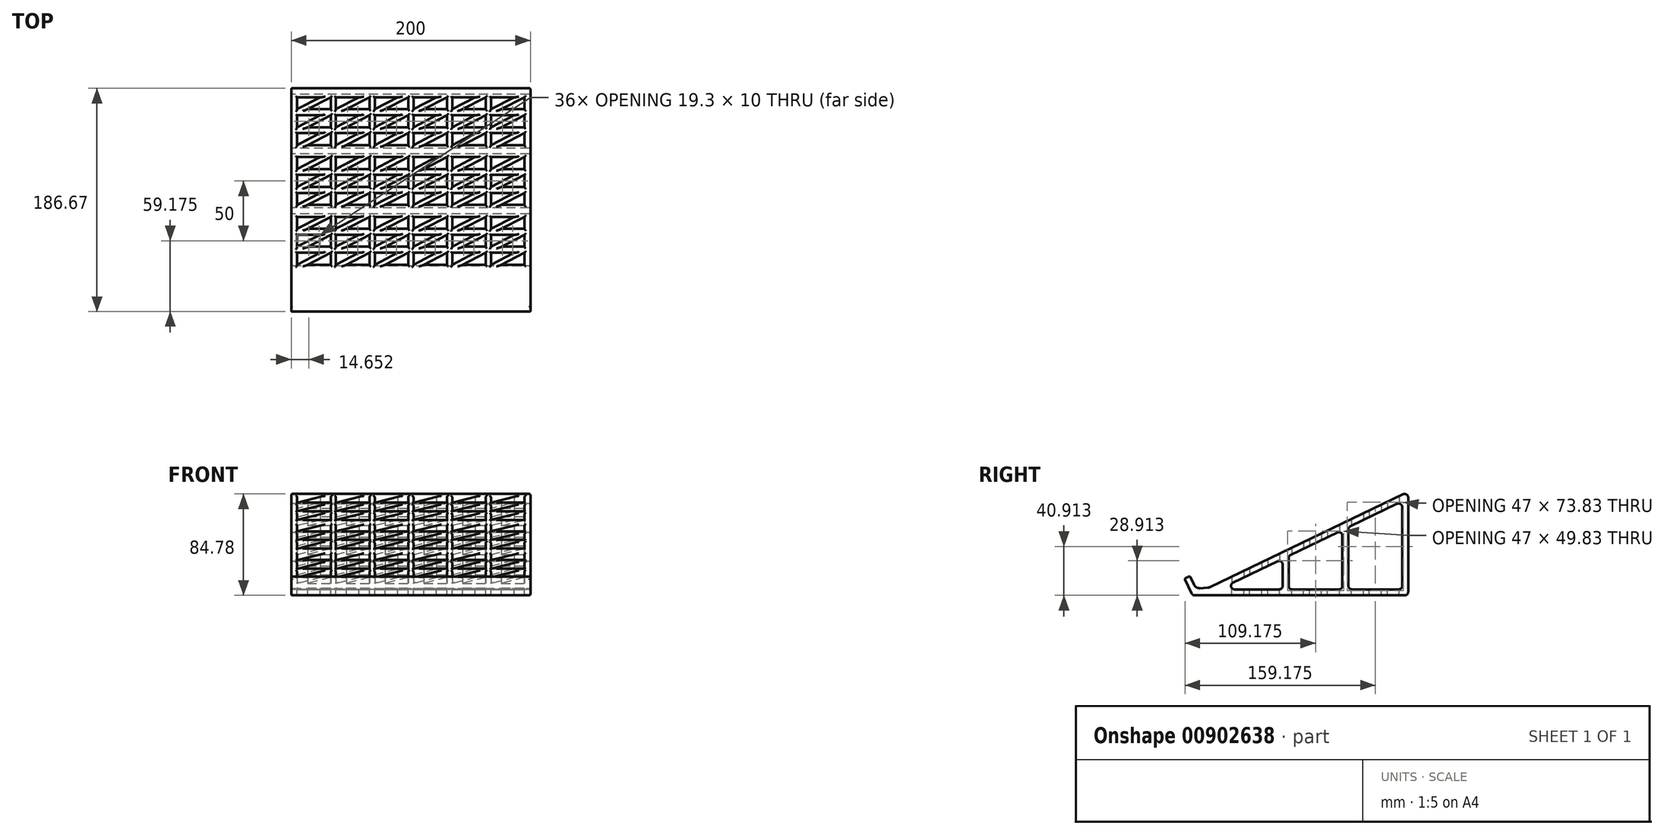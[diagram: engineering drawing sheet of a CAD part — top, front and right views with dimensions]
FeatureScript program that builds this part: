
annotation { "Feature Type Name" : "Feature", "Feature Type Description" : "" }
export const myFeature = defineFeature(function(context is Context, id is Id, definition is map)
    precondition{}
    {
        {
            var Q0;
            Q0=qCreatedBy(makeId("Right.planeOp"),FACE);
            var sketch = newSketch(context, id + "F0", { "sketchPlane" : qUnion([Q0])});
            skLineSegment(sketch, "E0", {"start": v(0, 0) * mm, "end": v(250, 120) * mm});
            skLineSegment(sketch, "E1", {"start": v(250, 120) * mm, "end": v(242.21, 136.23) * mm});
            skLineSegment(sketch, "E2", {"start": v(242.21, 136.23) * mm, "end": v(-7.79, 16.23) * mm});
            skLineSegment(sketch, "E3", {"start": v(-7.79, 16.23) * mm, "end": v(0, 0) * mm});
            skSolve(sketch);
        }
        {
            var Q0;
            Q0=qCreatedBy(makeId("Right.planeOp"),FACE);
            var sketch = newSketch(context, id + "F1", { "sketchPlane" : qUnion([Q0])});
            skLineSegment(sketch, "E4", {"start": v(0, 0) * mm, "end": v(180.3, 86.55) * mm});
            skLineSegment(sketch, "E5", {"start": v(180.3, 86.55) * mm, "end": v(180.3, 0) * mm});
            skLineSegment(sketch, "E6", {"start": v(180.3, 0) * mm, "end": v(0, 0) * mm});
            skLineSegment(sketch, "E7", {"start": v(0, 0) * mm, "end": v(-6.7, 13.97) * mm});
            skLineSegment(sketch, "E8", {"start": v(-6.7, 13.97) * mm, "end": v(-2.2, 16.14) * mm});
            skLineSegment(sketch, "E9", {"start": v(-2.2, 16.14) * mm, "end": v(4.5, 2.16) * mm});
            skLineSegment(sketch, "E10", {"start": v(75.3, 30.6) * mm, "end": v(75.3, 5) * mm});
            skLineSegment(sketch, "E11", {"start": v(75.3, 5) * mm, "end": v(21.97, 5) * mm});
            skLineSegment(sketch, "E12", {"start": v(21.97, 5) * mm, "end": v(75.3, 30.6) * mm});
            skLineSegment(sketch, "E13", {"start": v(175.3, 78.6) * mm, "end": v(130.3, 57) * mm});
            skLineSegment(sketch, "E14", {"start": v(175.3, 5) * mm, "end": v(175.3, 78.6) * mm});
            skLineSegment(sketch, "E15", {"start": v(125.3, 54.6) * mm, "end": v(125.3, 5) * mm});
            skLineSegment(sketch, "E16", {"start": v(80.3, 5) * mm, "end": v(125.3, 5) * mm});
            skLineSegment(sketch, "E17", {"start": v(80.3, 5) * mm, "end": v(80.3, 33) * mm});
            skLineSegment(sketch, "E18", {"start": v(80.3, 33) * mm, "end": v(125.3, 54.6) * mm});
            skLineSegment(sketch, "E19", {"start": v(130.3, 57) * mm, "end": v(130.3, 5) * mm});
            skLineSegment(sketch, "E20", {"start": v(130.3, 5) * mm, "end": v(175.3, 5) * mm});
            skSolve(sketch);
        }
        {
            var Q0;
            Q0=makeQuery(id+"F1.imprint","IMPRINT",FACE,{"disambiguationData":[TD([[makeQuery(id+"F1.imprint","IMPRINT",EDGE,{"derivedFrom":sQuery(id+"F1.wireOp",EDGE,"E4")}),-1.0]])]});
            var Q1;
            {var subQ0=sQuery(id+"F1.wireOp",EDGE,"E7");Q1=makeQuery(id+"F1.imprint","IMPRINT",FACE,{"disambiguationData":[TD([[makeQuery(id+"F1.imprint","IMPRINT",EDGE,{"derivedFrom":subQ0}),-1.0]])]});}
            extrude(context, id + "F2", {"entities" : qUnion([Q0, Q1]), "endBound" : BoundingType.SYMMETRIC, "depth" : 200 * mm, "offsetDistance" : 25 * mm});
        }
        {
            var Q0;
            Q0=makeQuery(id+"F2.opExtrude","SWEPT_FACE",FACE,{"disambiguationData":[OSD([sQuery(id+"F1.wireOp",EDGE,"E20")])]});
            var sketch = newSketch(context, id + "F3", { "sketchPlane" : qUnion([Q0])});
            skLineSegment(sketch, "E21", {"start": v(-95, 162.8) * mm, "end": v(-95, 172.8) * mm});
            skLineSegment(sketch, "E22", {"start": v(-95, 172.8) * mm, "end": v(-75.7, 172.8) * mm});
            skLineSegment(sketch, "E23", {"start": v(-75.7, 172.8) * mm, "end": v(-95, 162.8) * mm});
            skLineSegment(sketch, "E24", {"start": v(-86.3, 162.8) * mm, "end": v(-67, 172.8) * mm});
            skLineSegment(sketch, "E25", {"start": v(-67, 172.8) * mm, "end": v(-67, 162.8) * mm});
            skLineSegment(sketch, "E26", {"start": v(-67, 162.8) * mm, "end": v(-86.3, 162.8) * mm});
            skLineSegment(sketch, "E27.0.1.0", {"start": v(-67, 147.8) * mm, "end": v(-86.3, 147.8) * mm});
            skLineSegment(sketch, "E27.0.1.1", {"start": v(-86.3, 147.8) * mm, "end": v(-67, 157.8) * mm});
            skLineSegment(sketch, "E27.0.1.2", {"start": v(-95, 157.8) * mm, "end": v(-75.7, 157.8) * mm});
            skLineSegment(sketch, "E27.0.1.3", {"start": v(-75.7, 157.8) * mm, "end": v(-95, 147.8) * mm});
            skLineSegment(sketch, "E27.0.1.4", {"start": v(-67, 157.8) * mm, "end": v(-67, 147.8) * mm});
            skLineSegment(sketch, "E27.0.1.5", {"start": v(-95, 147.8) * mm, "end": v(-95, 157.8) * mm});
            skLineSegment(sketch, "E27.0.2.0", {"start": v(-67, 132.8) * mm, "end": v(-86.3, 132.8) * mm});
            skLineSegment(sketch, "E27.0.2.1", {"start": v(-86.3, 132.8) * mm, "end": v(-67, 142.8) * mm});
            skLineSegment(sketch, "E27.0.2.2", {"start": v(-95, 142.8) * mm, "end": v(-75.7, 142.8) * mm});
            skLineSegment(sketch, "E27.0.2.3", {"start": v(-75.7, 142.8) * mm, "end": v(-95, 132.8) * mm});
            skLineSegment(sketch, "E27.0.2.4", {"start": v(-67, 142.8) * mm, "end": v(-67, 132.8) * mm});
            skLineSegment(sketch, "E27.0.2.5", {"start": v(-95, 132.8) * mm, "end": v(-95, 142.8) * mm});
            skLineSegment(sketch, "E27.1.0.0", {"start": v(-34.6, 162.8) * mm, "end": v(-53.9, 162.8) * mm});
            skLineSegment(sketch, "E27.1.0.1", {"start": v(-53.9, 162.8) * mm, "end": v(-34.6, 172.8) * mm});
            skLineSegment(sketch, "E27.1.0.2", {"start": v(-62.6, 172.8) * mm, "end": v(-43.3, 172.8) * mm});
            skLineSegment(sketch, "E27.1.0.3", {"start": v(-43.3, 172.8) * mm, "end": v(-62.6, 162.8) * mm});
            skLineSegment(sketch, "E27.1.0.4", {"start": v(-34.6, 172.8) * mm, "end": v(-34.6, 162.8) * mm});
            skLineSegment(sketch, "E27.1.0.5", {"start": v(-62.6, 162.8) * mm, "end": v(-62.6, 172.8) * mm});
            skLineSegment(sketch, "E27.1.1.0", {"start": v(-34.6, 147.8) * mm, "end": v(-53.9, 147.8) * mm});
            skLineSegment(sketch, "E27.1.1.1", {"start": v(-53.9, 147.8) * mm, "end": v(-34.6, 157.8) * mm});
            skLineSegment(sketch, "E27.1.1.2", {"start": v(-62.6, 157.8) * mm, "end": v(-43.3, 157.8) * mm});
            skLineSegment(sketch, "E27.1.1.3", {"start": v(-43.3, 157.8) * mm, "end": v(-62.6, 147.8) * mm});
            skLineSegment(sketch, "E27.1.1.4", {"start": v(-34.6, 157.8) * mm, "end": v(-34.6, 147.8) * mm});
            skLineSegment(sketch, "E27.1.1.5", {"start": v(-62.6, 147.8) * mm, "end": v(-62.6, 157.8) * mm});
            skLineSegment(sketch, "E27.1.2.0", {"start": v(-34.6, 132.8) * mm, "end": v(-53.9, 132.8) * mm});
            skLineSegment(sketch, "E27.1.2.1", {"start": v(-53.9, 132.8) * mm, "end": v(-34.6, 142.8) * mm});
            skLineSegment(sketch, "E27.1.2.2", {"start": v(-62.6, 142.8) * mm, "end": v(-43.3, 142.8) * mm});
            skLineSegment(sketch, "E27.1.2.3", {"start": v(-43.3, 142.8) * mm, "end": v(-62.6, 132.8) * mm});
            skLineSegment(sketch, "E27.1.2.4", {"start": v(-34.6, 142.8) * mm, "end": v(-34.6, 132.8) * mm});
            skLineSegment(sketch, "E27.1.2.5", {"start": v(-62.6, 132.8) * mm, "end": v(-62.6, 142.8) * mm});
            skLineSegment(sketch, "E27.2.0.0", {"start": v(-2.2, 162.8) * mm, "end": v(-21.5, 162.8) * mm});
            skLineSegment(sketch, "E27.2.0.1", {"start": v(-21.5, 162.8) * mm, "end": v(-2.2, 172.8) * mm});
            skLineSegment(sketch, "E27.2.0.2", {"start": v(-30.2, 172.8) * mm, "end": v(-10.9, 172.8) * mm});
            skLineSegment(sketch, "E27.2.0.3", {"start": v(-10.9, 172.8) * mm, "end": v(-30.2, 162.8) * mm});
            skLineSegment(sketch, "E27.2.0.4", {"start": v(-2.2, 172.8) * mm, "end": v(-2.2, 162.8) * mm});
            skLineSegment(sketch, "E27.2.0.5", {"start": v(-30.2, 162.8) * mm, "end": v(-30.2, 172.8) * mm});
            skLineSegment(sketch, "E27.2.1.0", {"start": v(-2.2, 147.8) * mm, "end": v(-21.5, 147.8) * mm});
            skLineSegment(sketch, "E27.2.1.1", {"start": v(-21.5, 147.8) * mm, "end": v(-2.2, 157.8) * mm});
            skLineSegment(sketch, "E27.2.1.2", {"start": v(-30.2, 157.8) * mm, "end": v(-10.9, 157.8) * mm});
            skLineSegment(sketch, "E27.2.1.3", {"start": v(-10.9, 157.8) * mm, "end": v(-30.2, 147.8) * mm});
            skLineSegment(sketch, "E27.2.1.4", {"start": v(-2.2, 157.8) * mm, "end": v(-2.2, 147.8) * mm});
            skLineSegment(sketch, "E27.2.1.5", {"start": v(-30.2, 147.8) * mm, "end": v(-30.2, 157.8) * mm});
            skLineSegment(sketch, "E27.2.2.0", {"start": v(-2.2, 132.8) * mm, "end": v(-21.5, 132.8) * mm});
            skLineSegment(sketch, "E27.2.2.1", {"start": v(-21.5, 132.8) * mm, "end": v(-2.2, 142.8) * mm});
            skLineSegment(sketch, "E27.2.2.2", {"start": v(-30.2, 142.8) * mm, "end": v(-10.9, 142.8) * mm});
            skLineSegment(sketch, "E27.2.2.3", {"start": v(-10.9, 142.8) * mm, "end": v(-30.2, 132.8) * mm});
            skLineSegment(sketch, "E27.2.2.4", {"start": v(-2.2, 142.8) * mm, "end": v(-2.2, 132.8) * mm});
            skLineSegment(sketch, "E27.2.2.5", {"start": v(-30.2, 132.8) * mm, "end": v(-30.2, 142.8) * mm});
            skLineSegment(sketch, "E27.3.0.0", {"start": v(30.2, 162.8) * mm, "end": v(10.9, 162.8) * mm});
            skLineSegment(sketch, "E27.3.0.1", {"start": v(10.9, 162.8) * mm, "end": v(30.2, 172.8) * mm});
            skLineSegment(sketch, "E27.3.0.2", {"start": v(2.2, 172.8) * mm, "end": v(21.5, 172.8) * mm});
            skLineSegment(sketch, "E27.3.0.3", {"start": v(21.5, 172.8) * mm, "end": v(2.2, 162.8) * mm});
            skLineSegment(sketch, "E27.3.0.4", {"start": v(30.2, 172.8) * mm, "end": v(30.2, 162.8) * mm});
            skLineSegment(sketch, "E27.3.0.5", {"start": v(2.2, 162.8) * mm, "end": v(2.2, 172.8) * mm});
            skLineSegment(sketch, "E27.3.1.0", {"start": v(30.2, 147.8) * mm, "end": v(10.9, 147.8) * mm});
            skLineSegment(sketch, "E27.3.1.1", {"start": v(10.9, 147.8) * mm, "end": v(30.2, 157.8) * mm});
            skLineSegment(sketch, "E27.3.1.2", {"start": v(2.2, 157.8) * mm, "end": v(21.5, 157.8) * mm});
            skLineSegment(sketch, "E27.3.1.3", {"start": v(21.5, 157.8) * mm, "end": v(2.2, 147.8) * mm});
            skLineSegment(sketch, "E27.3.1.4", {"start": v(30.2, 157.8) * mm, "end": v(30.2, 147.8) * mm});
            skLineSegment(sketch, "E27.3.1.5", {"start": v(2.2, 147.8) * mm, "end": v(2.2, 157.8) * mm});
            skLineSegment(sketch, "E27.3.2.0", {"start": v(30.2, 132.8) * mm, "end": v(10.9, 132.8) * mm});
            skLineSegment(sketch, "E27.3.2.1", {"start": v(10.9, 132.8) * mm, "end": v(30.2, 142.8) * mm});
            skLineSegment(sketch, "E27.3.2.2", {"start": v(2.2, 142.8) * mm, "end": v(21.5, 142.8) * mm});
            skLineSegment(sketch, "E27.3.2.3", {"start": v(21.5, 142.8) * mm, "end": v(2.2, 132.8) * mm});
            skLineSegment(sketch, "E27.3.2.4", {"start": v(30.2, 142.8) * mm, "end": v(30.2, 132.8) * mm});
            skLineSegment(sketch, "E27.3.2.5", {"start": v(2.2, 132.8) * mm, "end": v(2.2, 142.8) * mm});
            skLineSegment(sketch, "E27.4.0.0", {"start": v(62.6, 162.8) * mm, "end": v(43.3, 162.8) * mm});
            skLineSegment(sketch, "E27.4.0.1", {"start": v(43.3, 162.8) * mm, "end": v(62.6, 172.8) * mm});
            skLineSegment(sketch, "E27.4.0.2", {"start": v(34.6, 172.8) * mm, "end": v(53.9, 172.8) * mm});
            skLineSegment(sketch, "E27.4.0.3", {"start": v(53.9, 172.8) * mm, "end": v(34.6, 162.8) * mm});
            skLineSegment(sketch, "E27.4.0.4", {"start": v(62.6, 172.8) * mm, "end": v(62.6, 162.8) * mm});
            skLineSegment(sketch, "E27.4.0.5", {"start": v(34.6, 162.8) * mm, "end": v(34.6, 172.8) * mm});
            skLineSegment(sketch, "E27.4.1.0", {"start": v(62.6, 147.8) * mm, "end": v(43.3, 147.8) * mm});
            skLineSegment(sketch, "E27.4.1.1", {"start": v(43.3, 147.8) * mm, "end": v(62.6, 157.8) * mm});
            skLineSegment(sketch, "E27.4.1.2", {"start": v(34.6, 157.8) * mm, "end": v(53.9, 157.8) * mm});
            skLineSegment(sketch, "E27.4.1.3", {"start": v(53.9, 157.8) * mm, "end": v(34.6, 147.8) * mm});
            skLineSegment(sketch, "E27.4.1.4", {"start": v(62.6, 157.8) * mm, "end": v(62.6, 147.8) * mm});
            skLineSegment(sketch, "E27.4.1.5", {"start": v(34.6, 147.8) * mm, "end": v(34.6, 157.8) * mm});
            skLineSegment(sketch, "E27.4.2.0", {"start": v(62.6, 132.8) * mm, "end": v(43.3, 132.8) * mm});
            skLineSegment(sketch, "E27.4.2.1", {"start": v(43.3, 132.8) * mm, "end": v(62.6, 142.8) * mm});
            skLineSegment(sketch, "E27.4.2.2", {"start": v(34.6, 142.8) * mm, "end": v(53.9, 142.8) * mm});
            skLineSegment(sketch, "E27.4.2.3", {"start": v(53.9, 142.8) * mm, "end": v(34.6, 132.8) * mm});
            skLineSegment(sketch, "E27.4.2.4", {"start": v(62.6, 142.8) * mm, "end": v(62.6, 132.8) * mm});
            skLineSegment(sketch, "E27.4.2.5", {"start": v(34.6, 132.8) * mm, "end": v(34.6, 142.8) * mm});
            skLineSegment(sketch, "E27.5.0.0", {"start": v(95, 162.8) * mm, "end": v(75.7, 162.8) * mm});
            skLineSegment(sketch, "E27.5.0.1", {"start": v(75.7, 162.8) * mm, "end": v(95, 172.8) * mm});
            skLineSegment(sketch, "E27.5.0.2", {"start": v(67, 172.8) * mm, "end": v(86.3, 172.8) * mm});
            skLineSegment(sketch, "E27.5.0.3", {"start": v(86.3, 172.8) * mm, "end": v(67, 162.8) * mm});
            skLineSegment(sketch, "E27.5.0.4", {"start": v(95, 172.8) * mm, "end": v(95, 162.8) * mm});
            skLineSegment(sketch, "E27.5.0.5", {"start": v(67, 162.8) * mm, "end": v(67, 172.8) * mm});
            skLineSegment(sketch, "E27.5.1.0", {"start": v(95, 147.8) * mm, "end": v(75.7, 147.8) * mm});
            skLineSegment(sketch, "E27.5.1.1", {"start": v(75.7, 147.8) * mm, "end": v(95, 157.8) * mm});
            skLineSegment(sketch, "E27.5.1.2", {"start": v(67, 157.8) * mm, "end": v(86.3, 157.8) * mm});
            skLineSegment(sketch, "E27.5.1.3", {"start": v(86.3, 157.8) * mm, "end": v(67, 147.8) * mm});
            skLineSegment(sketch, "E27.5.1.4", {"start": v(95, 157.8) * mm, "end": v(95, 147.8) * mm});
            skLineSegment(sketch, "E27.5.1.5", {"start": v(67, 147.8) * mm, "end": v(67, 157.8) * mm});
            skLineSegment(sketch, "E27.5.2.0", {"start": v(95, 132.8) * mm, "end": v(75.7, 132.8) * mm});
            skLineSegment(sketch, "E27.5.2.1", {"start": v(75.7, 132.8) * mm, "end": v(95, 142.8) * mm});
            skLineSegment(sketch, "E27.5.2.2", {"start": v(67, 142.8) * mm, "end": v(86.3, 142.8) * mm});
            skLineSegment(sketch, "E27.5.2.3", {"start": v(86.3, 142.8) * mm, "end": v(67, 132.8) * mm});
            skLineSegment(sketch, "E27.5.2.4", {"start": v(95, 142.8) * mm, "end": v(95, 132.8) * mm});
            skLineSegment(sketch, "E27.5.2.5", {"start": v(67, 132.8) * mm, "end": v(67, 142.8) * mm});
            skLineSegment(sketch, "E27.direction1", {"start": v(-95, 162.8) * mm, "end": v(-62.6, 162.8) * mm, "construction": true});
            skLineSegment(sketch, "E27.direction2", {"start": v(-95, 162.8) * mm, "end": v(-95, 147.8) * mm, "construction": true});
            skLineSegment(sketch, "E28.0.1.0", {"start": v(34.6, 112.8) * mm, "end": v(34.6, 122.8) * mm});
            skLineSegment(sketch, "E28.0.1.1", {"start": v(-34.6, 82.8) * mm, "end": v(-53.9, 82.8) * mm});
            skLineSegment(sketch, "E28.0.1.2", {"start": v(-10.9, 92.8) * mm, "end": v(-30.2, 82.8) * mm});
            skLineSegment(sketch, "E28.0.1.3", {"start": v(34.6, 82.8) * mm, "end": v(34.6, 92.8) * mm});
            skLineSegment(sketch, "E28.0.1.4", {"start": v(-2.2, 97.8) * mm, "end": v(-21.5, 97.8) * mm});
            skLineSegment(sketch, "E28.0.1.5", {"start": v(-75.7, 107.8) * mm, "end": v(-95, 97.8) * mm});
            skLineSegment(sketch, "E28.0.1.6", {"start": v(-95, 122.8) * mm, "end": v(-75.7, 122.8) * mm});
            skLineSegment(sketch, "E28.0.1.7", {"start": v(30.2, 112.8) * mm, "end": v(10.9, 112.8) * mm});
            skLineSegment(sketch, "E28.0.1.8", {"start": v(-2.2, 92.8) * mm, "end": v(-2.2, 82.8) * mm});
            skLineSegment(sketch, "E28.0.1.9", {"start": v(-86.3, 112.8) * mm, "end": v(-67, 122.8) * mm});
            skLineSegment(sketch, "E28.0.1.10", {"start": v(-34.6, 107.8) * mm, "end": v(-34.6, 97.8) * mm});
            skLineSegment(sketch, "E28.0.1.11", {"start": v(-62.6, 97.8) * mm, "end": v(-62.6, 107.8) * mm});
            skLineSegment(sketch, "E28.0.1.12", {"start": v(62.6, 112.8) * mm, "end": v(43.3, 112.8) * mm});
            skLineSegment(sketch, "E28.0.1.13", {"start": v(-34.6, 97.8) * mm, "end": v(-53.9, 97.8) * mm});
            skLineSegment(sketch, "E28.0.1.14", {"start": v(-30.2, 82.8) * mm, "end": v(-30.2, 92.8) * mm});
            skLineSegment(sketch, "E28.0.1.15", {"start": v(2.2, 97.8) * mm, "end": v(2.2, 107.8) * mm});
            skLineSegment(sketch, "E28.0.1.16", {"start": v(-43.3, 107.8) * mm, "end": v(-62.6, 97.8) * mm});
            skLineSegment(sketch, "E28.0.1.17", {"start": v(-30.2, 112.8) * mm, "end": v(-30.2, 122.8) * mm});
            skLineSegment(sketch, "E28.0.1.18", {"start": v(30.2, 122.8) * mm, "end": v(30.2, 112.8) * mm});
            skLineSegment(sketch, "E28.0.1.19", {"start": v(-67, 122.8) * mm, "end": v(-67, 112.8) * mm});
            skLineSegment(sketch, "E28.0.1.20", {"start": v(95, 107.8) * mm, "end": v(95, 97.8) * mm});
            skLineSegment(sketch, "E28.0.1.21", {"start": v(-2.2, 112.8) * mm, "end": v(-21.5, 112.8) * mm});
            skLineSegment(sketch, "E28.0.1.22", {"start": v(62.6, 107.8) * mm, "end": v(62.6, 97.8) * mm});
            skLineSegment(sketch, "E28.0.1.23", {"start": v(30.2, 97.8) * mm, "end": v(10.9, 97.8) * mm});
            skLineSegment(sketch, "E28.0.1.24", {"start": v(67, 107.8) * mm, "end": v(86.3, 107.8) * mm});
            skLineSegment(sketch, "E28.0.1.25", {"start": v(34.6, 122.8) * mm, "end": v(53.9, 122.8) * mm});
            skLineSegment(sketch, "E28.0.1.26", {"start": v(-75.7, 92.8) * mm, "end": v(-95, 82.8) * mm});
            skLineSegment(sketch, "E28.0.1.27", {"start": v(53.9, 92.8) * mm, "end": v(34.6, 82.8) * mm});
            skLineSegment(sketch, "E28.0.1.28", {"start": v(2.2, 92.8) * mm, "end": v(21.5, 92.8) * mm});
            skLineSegment(sketch, "E28.0.1.29", {"start": v(-86.3, 97.8) * mm, "end": v(-67, 107.8) * mm});
            skLineSegment(sketch, "E28.0.1.30", {"start": v(-95, 112.8) * mm, "end": v(-95, 122.8) * mm});
            skLineSegment(sketch, "E28.0.1.31", {"start": v(-95, 112.8) * mm, "end": v(-62.6, 112.8) * mm, "construction": true});
            skLineSegment(sketch, "E28.0.1.32", {"start": v(-10.9, 107.8) * mm, "end": v(-30.2, 97.8) * mm});
            skLineSegment(sketch, "E28.0.1.33", {"start": v(-10.9, 122.8) * mm, "end": v(-30.2, 112.8) * mm});
            skLineSegment(sketch, "E28.0.1.34", {"start": v(43.3, 82.8) * mm, "end": v(62.6, 92.8) * mm});
            skLineSegment(sketch, "E28.0.1.35", {"start": v(43.3, 112.8) * mm, "end": v(62.6, 122.8) * mm});
            skLineSegment(sketch, "E28.0.1.36", {"start": v(-43.3, 92.8) * mm, "end": v(-62.6, 82.8) * mm});
            skLineSegment(sketch, "E28.0.1.37", {"start": v(86.3, 122.8) * mm, "end": v(67, 112.8) * mm});
            skLineSegment(sketch, "E28.0.1.38", {"start": v(2.2, 122.8) * mm, "end": v(21.5, 122.8) * mm});
            skLineSegment(sketch, "E28.0.1.39", {"start": v(67, 112.8) * mm, "end": v(67, 122.8) * mm});
            skLineSegment(sketch, "E28.0.1.40", {"start": v(-30.2, 107.8) * mm, "end": v(-10.9, 107.8) * mm});
            skLineSegment(sketch, "E28.0.1.41", {"start": v(-30.2, 122.8) * mm, "end": v(-10.9, 122.8) * mm});
            skLineSegment(sketch, "E28.0.1.42", {"start": v(-95, 92.8) * mm, "end": v(-75.7, 92.8) * mm});
            skLineSegment(sketch, "E28.0.1.43", {"start": v(62.6, 97.8) * mm, "end": v(43.3, 97.8) * mm});
            skLineSegment(sketch, "E28.0.1.44", {"start": v(-67, 92.8) * mm, "end": v(-67, 82.8) * mm});
            skLineSegment(sketch, "E28.0.1.45", {"start": v(-67, 107.8) * mm, "end": v(-67, 97.8) * mm});
            skLineSegment(sketch, "E28.0.1.46", {"start": v(-21.5, 82.8) * mm, "end": v(-2.2, 92.8) * mm});
            skLineSegment(sketch, "E28.0.1.47", {"start": v(86.3, 92.8) * mm, "end": v(67, 82.8) * mm});
            skLineSegment(sketch, "E28.0.1.48", {"start": v(-30.2, 92.8) * mm, "end": v(-10.9, 92.8) * mm});
            skLineSegment(sketch, "E28.0.1.49", {"start": v(-62.6, 122.8) * mm, "end": v(-43.3, 122.8) * mm});
            skLineSegment(sketch, "E28.0.1.50", {"start": v(75.7, 97.8) * mm, "end": v(95, 107.8) * mm});
            skLineSegment(sketch, "E28.0.1.51", {"start": v(-34.6, 112.8) * mm, "end": v(-53.9, 112.8) * mm});
            skLineSegment(sketch, "E28.0.1.52", {"start": v(34.6, 97.8) * mm, "end": v(34.6, 107.8) * mm});
            skLineSegment(sketch, "E28.0.1.53", {"start": v(43.3, 97.8) * mm, "end": v(62.6, 107.8) * mm});
            skLineSegment(sketch, "E28.0.1.54", {"start": v(67, 92.8) * mm, "end": v(86.3, 92.8) * mm});
            skLineSegment(sketch, "E28.0.1.55", {"start": v(-30.2, 97.8) * mm, "end": v(-30.2, 107.8) * mm});
            skLineSegment(sketch, "E28.0.1.56", {"start": v(95, 97.8) * mm, "end": v(75.7, 97.8) * mm});
            skLineSegment(sketch, "E28.0.1.57", {"start": v(95, 92.8) * mm, "end": v(95, 82.8) * mm});
            skLineSegment(sketch, "E28.0.1.58", {"start": v(34.6, 92.8) * mm, "end": v(53.9, 92.8) * mm});
            skLineSegment(sketch, "E28.0.1.59", {"start": v(-62.6, 92.8) * mm, "end": v(-43.3, 92.8) * mm});
            skLineSegment(sketch, "E28.0.1.60", {"start": v(10.9, 82.8) * mm, "end": v(30.2, 92.8) * mm});
            skLineSegment(sketch, "E28.0.1.61", {"start": v(86.3, 107.8) * mm, "end": v(67, 97.8) * mm});
            skLineSegment(sketch, "E28.0.1.62", {"start": v(34.6, 107.8) * mm, "end": v(53.9, 107.8) * mm});
            skLineSegment(sketch, "E28.0.1.63", {"start": v(10.9, 97.8) * mm, "end": v(30.2, 107.8) * mm});
            skLineSegment(sketch, "E28.0.1.64", {"start": v(-95, 107.8) * mm, "end": v(-75.7, 107.8) * mm});
            skLineSegment(sketch, "E28.0.1.65", {"start": v(21.5, 122.8) * mm, "end": v(2.2, 112.8) * mm});
            skLineSegment(sketch, "E28.0.1.66", {"start": v(-75.7, 122.8) * mm, "end": v(-95, 112.8) * mm});
            skLineSegment(sketch, "E28.0.1.67", {"start": v(-34.6, 92.8) * mm, "end": v(-34.6, 82.8) * mm});
            skLineSegment(sketch, "E28.0.1.68", {"start": v(21.5, 107.8) * mm, "end": v(2.2, 97.8) * mm});
            skLineSegment(sketch, "E28.0.1.69", {"start": v(30.2, 107.8) * mm, "end": v(30.2, 97.8) * mm});
            skLineSegment(sketch, "E28.0.1.70", {"start": v(2.2, 112.8) * mm, "end": v(2.2, 122.8) * mm});
            skLineSegment(sketch, "E28.0.1.71", {"start": v(-62.6, 107.8) * mm, "end": v(-43.3, 107.8) * mm});
            skLineSegment(sketch, "E28.0.1.72", {"start": v(-67, 97.8) * mm, "end": v(-86.3, 97.8) * mm});
            skLineSegment(sketch, "E28.0.1.73", {"start": v(67, 82.8) * mm, "end": v(67, 92.8) * mm});
            skLineSegment(sketch, "E28.0.1.74", {"start": v(-95, 82.8) * mm, "end": v(-95, 92.8) * mm});
            skLineSegment(sketch, "E28.0.1.75", {"start": v(62.6, 122.8) * mm, "end": v(62.6, 112.8) * mm});
            skLineSegment(sketch, "E28.0.1.76", {"start": v(67, 122.8) * mm, "end": v(86.3, 122.8) * mm});
            skLineSegment(sketch, "E28.0.1.77", {"start": v(-43.3, 122.8) * mm, "end": v(-62.6, 112.8) * mm});
            skLineSegment(sketch, "E28.0.1.78", {"start": v(95, 112.8) * mm, "end": v(75.7, 112.8) * mm});
            skLineSegment(sketch, "E28.0.1.79", {"start": v(30.2, 82.8) * mm, "end": v(10.9, 82.8) * mm});
            skLineSegment(sketch, "E28.0.1.80", {"start": v(-86.3, 82.8) * mm, "end": v(-67, 92.8) * mm});
            skLineSegment(sketch, "E28.0.1.81", {"start": v(-2.2, 82.8) * mm, "end": v(-21.5, 82.8) * mm});
            skLineSegment(sketch, "E28.0.1.82", {"start": v(62.6, 82.8) * mm, "end": v(43.3, 82.8) * mm});
            skLineSegment(sketch, "E28.0.1.83", {"start": v(-34.6, 122.8) * mm, "end": v(-34.6, 112.8) * mm});
            skLineSegment(sketch, "E28.0.1.84", {"start": v(53.9, 107.8) * mm, "end": v(34.6, 97.8) * mm});
            skLineSegment(sketch, "E28.0.1.85", {"start": v(-53.9, 97.8) * mm, "end": v(-34.6, 107.8) * mm});
            skLineSegment(sketch, "E28.0.1.86", {"start": v(75.7, 112.8) * mm, "end": v(95, 122.8) * mm});
            skLineSegment(sketch, "E28.0.1.87", {"start": v(67, 97.8) * mm, "end": v(67, 107.8) * mm});
            skLineSegment(sketch, "E28.0.1.88", {"start": v(2.2, 82.8) * mm, "end": v(2.2, 92.8) * mm});
            skLineSegment(sketch, "E28.0.1.89", {"start": v(-2.2, 122.8) * mm, "end": v(-2.2, 112.8) * mm});
            skLineSegment(sketch, "E28.0.1.90", {"start": v(30.2, 92.8) * mm, "end": v(30.2, 82.8) * mm});
            skLineSegment(sketch, "E28.0.1.91", {"start": v(95, 82.8) * mm, "end": v(75.7, 82.8) * mm});
            skLineSegment(sketch, "E28.0.1.92", {"start": v(-95, 112.8) * mm, "end": v(-95, 97.8) * mm, "construction": true});
            skLineSegment(sketch, "E28.0.1.93", {"start": v(-53.9, 112.8) * mm, "end": v(-34.6, 122.8) * mm});
            skLineSegment(sketch, "E28.0.1.94", {"start": v(-21.5, 112.8) * mm, "end": v(-2.2, 122.8) * mm});
            skLineSegment(sketch, "E28.0.1.95", {"start": v(-62.6, 112.8) * mm, "end": v(-62.6, 122.8) * mm});
            skLineSegment(sketch, "E28.0.1.96", {"start": v(21.5, 92.8) * mm, "end": v(2.2, 82.8) * mm});
            skLineSegment(sketch, "E28.0.1.97", {"start": v(-53.9, 82.8) * mm, "end": v(-34.6, 92.8) * mm});
            skLineSegment(sketch, "E28.0.1.98", {"start": v(2.2, 107.8) * mm, "end": v(21.5, 107.8) * mm});
            skLineSegment(sketch, "E28.0.1.99", {"start": v(62.6, 92.8) * mm, "end": v(62.6, 82.8) * mm});
            skLineSegment(sketch, "E28.0.1.100", {"start": v(-67, 82.8) * mm, "end": v(-86.3, 82.8) * mm});
            skLineSegment(sketch, "E28.0.1.101", {"start": v(53.9, 122.8) * mm, "end": v(34.6, 112.8) * mm});
            skLineSegment(sketch, "E28.0.1.102", {"start": v(-21.5, 97.8) * mm, "end": v(-2.2, 107.8) * mm});
            skLineSegment(sketch, "E28.0.1.103", {"start": v(95, 122.8) * mm, "end": v(95, 112.8) * mm});
            skLineSegment(sketch, "E28.0.1.104", {"start": v(-62.6, 82.8) * mm, "end": v(-62.6, 92.8) * mm});
            skLineSegment(sketch, "E28.0.1.105", {"start": v(75.7, 82.8) * mm, "end": v(95, 92.8) * mm});
            skLineSegment(sketch, "E28.0.1.106", {"start": v(10.9, 112.8) * mm, "end": v(30.2, 122.8) * mm});
            skLineSegment(sketch, "E28.0.1.107", {"start": v(-2.2, 107.8) * mm, "end": v(-2.2, 97.8) * mm});
            skLineSegment(sketch, "E28.0.1.108", {"start": v(-67, 112.8) * mm, "end": v(-86.3, 112.8) * mm});
            skLineSegment(sketch, "E28.0.1.109", {"start": v(-95, 97.8) * mm, "end": v(-95, 107.8) * mm});
            skLineSegment(sketch, "E28.0.2.0", {"start": v(34.6, 62.8) * mm, "end": v(34.6, 72.8) * mm});
            skLineSegment(sketch, "E28.0.2.1", {"start": v(-34.6, 32.8) * mm, "end": v(-53.9, 32.8) * mm});
            skLineSegment(sketch, "E28.0.2.2", {"start": v(-10.9, 42.8) * mm, "end": v(-30.2, 32.8) * mm});
            skLineSegment(sketch, "E28.0.2.3", {"start": v(34.6, 32.8) * mm, "end": v(34.6, 42.8) * mm});
            skLineSegment(sketch, "E28.0.2.4", {"start": v(-2.2, 47.8) * mm, "end": v(-21.5, 47.8) * mm});
            skLineSegment(sketch, "E28.0.2.5", {"start": v(-75.7, 57.8) * mm, "end": v(-95, 47.8) * mm});
            skLineSegment(sketch, "E28.0.2.6", {"start": v(-95, 72.8) * mm, "end": v(-75.7, 72.8) * mm});
            skLineSegment(sketch, "E28.0.2.7", {"start": v(30.2, 62.8) * mm, "end": v(10.9, 62.8) * mm});
            skLineSegment(sketch, "E28.0.2.8", {"start": v(-2.2, 42.8) * mm, "end": v(-2.2, 32.8) * mm});
            skLineSegment(sketch, "E28.0.2.9", {"start": v(-86.3, 62.8) * mm, "end": v(-67, 72.8) * mm});
            skLineSegment(sketch, "E28.0.2.10", {"start": v(-34.6, 57.8) * mm, "end": v(-34.6, 47.8) * mm});
            skLineSegment(sketch, "E28.0.2.11", {"start": v(-62.6, 47.8) * mm, "end": v(-62.6, 57.8) * mm});
            skLineSegment(sketch, "E28.0.2.12", {"start": v(62.6, 62.8) * mm, "end": v(43.3, 62.8) * mm});
            skLineSegment(sketch, "E28.0.2.13", {"start": v(-34.6, 47.8) * mm, "end": v(-53.9, 47.8) * mm});
            skLineSegment(sketch, "E28.0.2.14", {"start": v(-30.2, 32.8) * mm, "end": v(-30.2, 42.8) * mm});
            skLineSegment(sketch, "E28.0.2.15", {"start": v(2.2, 47.8) * mm, "end": v(2.2, 57.8) * mm});
            skLineSegment(sketch, "E28.0.2.16", {"start": v(-43.3, 57.8) * mm, "end": v(-62.6, 47.8) * mm});
            skLineSegment(sketch, "E28.0.2.17", {"start": v(-30.2, 62.8) * mm, "end": v(-30.2, 72.8) * mm});
            skLineSegment(sketch, "E28.0.2.18", {"start": v(30.2, 72.8) * mm, "end": v(30.2, 62.8) * mm});
            skLineSegment(sketch, "E28.0.2.19", {"start": v(-67, 72.8) * mm, "end": v(-67, 62.8) * mm});
            skLineSegment(sketch, "E28.0.2.20", {"start": v(95, 57.8) * mm, "end": v(95, 47.8) * mm});
            skLineSegment(sketch, "E28.0.2.21", {"start": v(-2.2, 62.8) * mm, "end": v(-21.5, 62.8) * mm});
            skLineSegment(sketch, "E28.0.2.22", {"start": v(62.6, 57.8) * mm, "end": v(62.6, 47.8) * mm});
            skLineSegment(sketch, "E28.0.2.23", {"start": v(30.2, 47.8) * mm, "end": v(10.9, 47.8) * mm});
            skLineSegment(sketch, "E28.0.2.24", {"start": v(67, 57.8) * mm, "end": v(86.3, 57.8) * mm});
            skLineSegment(sketch, "E28.0.2.25", {"start": v(34.6, 72.8) * mm, "end": v(53.9, 72.8) * mm});
            skLineSegment(sketch, "E28.0.2.26", {"start": v(-75.7, 42.8) * mm, "end": v(-95, 32.8) * mm});
            skLineSegment(sketch, "E28.0.2.27", {"start": v(53.9, 42.8) * mm, "end": v(34.6, 32.8) * mm});
            skLineSegment(sketch, "E28.0.2.28", {"start": v(2.2, 42.8) * mm, "end": v(21.5, 42.8) * mm});
            skLineSegment(sketch, "E28.0.2.29", {"start": v(-86.3, 47.8) * mm, "end": v(-67, 57.8) * mm});
            skLineSegment(sketch, "E28.0.2.30", {"start": v(-95, 62.8) * mm, "end": v(-95, 72.8) * mm});
            skLineSegment(sketch, "E28.0.2.31", {"start": v(-95, 62.8) * mm, "end": v(-62.6, 62.8) * mm, "construction": true});
            skLineSegment(sketch, "E28.0.2.32", {"start": v(-10.9, 57.8) * mm, "end": v(-30.2, 47.8) * mm});
            skLineSegment(sketch, "E28.0.2.33", {"start": v(-10.9, 72.8) * mm, "end": v(-30.2, 62.8) * mm});
            skLineSegment(sketch, "E28.0.2.34", {"start": v(43.3, 32.8) * mm, "end": v(62.6, 42.8) * mm});
            skLineSegment(sketch, "E28.0.2.35", {"start": v(43.3, 62.8) * mm, "end": v(62.6, 72.8) * mm});
            skLineSegment(sketch, "E28.0.2.36", {"start": v(-43.3, 42.8) * mm, "end": v(-62.6, 32.8) * mm});
            skLineSegment(sketch, "E28.0.2.37", {"start": v(86.3, 72.8) * mm, "end": v(67, 62.8) * mm});
            skLineSegment(sketch, "E28.0.2.38", {"start": v(2.2, 72.8) * mm, "end": v(21.5, 72.8) * mm});
            skLineSegment(sketch, "E28.0.2.39", {"start": v(67, 62.8) * mm, "end": v(67, 72.8) * mm});
            skLineSegment(sketch, "E28.0.2.40", {"start": v(-30.2, 57.8) * mm, "end": v(-10.9, 57.8) * mm});
            skLineSegment(sketch, "E28.0.2.41", {"start": v(-30.2, 72.8) * mm, "end": v(-10.9, 72.8) * mm});
            skLineSegment(sketch, "E28.0.2.42", {"start": v(-95, 42.8) * mm, "end": v(-75.7, 42.8) * mm});
            skLineSegment(sketch, "E28.0.2.43", {"start": v(62.6, 47.8) * mm, "end": v(43.3, 47.8) * mm});
            skLineSegment(sketch, "E28.0.2.44", {"start": v(-67, 42.8) * mm, "end": v(-67, 32.8) * mm});
            skLineSegment(sketch, "E28.0.2.45", {"start": v(-67, 57.8) * mm, "end": v(-67, 47.8) * mm});
            skLineSegment(sketch, "E28.0.2.46", {"start": v(-21.5, 32.8) * mm, "end": v(-2.2, 42.8) * mm});
            skLineSegment(sketch, "E28.0.2.47", {"start": v(86.3, 42.8) * mm, "end": v(67, 32.8) * mm});
            skLineSegment(sketch, "E28.0.2.48", {"start": v(-30.2, 42.8) * mm, "end": v(-10.9, 42.8) * mm});
            skLineSegment(sketch, "E28.0.2.49", {"start": v(-62.6, 72.8) * mm, "end": v(-43.3, 72.8) * mm});
            skLineSegment(sketch, "E28.0.2.50", {"start": v(75.7, 47.8) * mm, "end": v(95, 57.8) * mm});
            skLineSegment(sketch, "E28.0.2.51", {"start": v(-34.6, 62.8) * mm, "end": v(-53.9, 62.8) * mm});
            skLineSegment(sketch, "E28.0.2.52", {"start": v(34.6, 47.8) * mm, "end": v(34.6, 57.8) * mm});
            skLineSegment(sketch, "E28.0.2.53", {"start": v(43.3, 47.8) * mm, "end": v(62.6, 57.8) * mm});
            skLineSegment(sketch, "E28.0.2.54", {"start": v(67, 42.8) * mm, "end": v(86.3, 42.8) * mm});
            skLineSegment(sketch, "E28.0.2.55", {"start": v(-30.2, 47.8) * mm, "end": v(-30.2, 57.8) * mm});
            skLineSegment(sketch, "E28.0.2.56", {"start": v(95, 47.8) * mm, "end": v(75.7, 47.8) * mm});
            skLineSegment(sketch, "E28.0.2.57", {"start": v(95, 42.8) * mm, "end": v(95, 32.8) * mm});
            skLineSegment(sketch, "E28.0.2.58", {"start": v(34.6, 42.8) * mm, "end": v(53.9, 42.8) * mm});
            skLineSegment(sketch, "E28.0.2.59", {"start": v(-62.6, 42.8) * mm, "end": v(-43.3, 42.8) * mm});
            skLineSegment(sketch, "E28.0.2.60", {"start": v(10.9, 32.8) * mm, "end": v(30.2, 42.8) * mm});
            skLineSegment(sketch, "E28.0.2.61", {"start": v(86.3, 57.8) * mm, "end": v(67, 47.8) * mm});
            skLineSegment(sketch, "E28.0.2.62", {"start": v(34.6, 57.8) * mm, "end": v(53.9, 57.8) * mm});
            skLineSegment(sketch, "E28.0.2.63", {"start": v(10.9, 47.8) * mm, "end": v(30.2, 57.8) * mm});
            skLineSegment(sketch, "E28.0.2.64", {"start": v(-95, 57.8) * mm, "end": v(-75.7, 57.8) * mm});
            skLineSegment(sketch, "E28.0.2.65", {"start": v(21.5, 72.8) * mm, "end": v(2.2, 62.8) * mm});
            skLineSegment(sketch, "E28.0.2.66", {"start": v(-75.7, 72.8) * mm, "end": v(-95, 62.8) * mm});
            skLineSegment(sketch, "E28.0.2.67", {"start": v(-34.6, 42.8) * mm, "end": v(-34.6, 32.8) * mm});
            skLineSegment(sketch, "E28.0.2.68", {"start": v(21.5, 57.8) * mm, "end": v(2.2, 47.8) * mm});
            skLineSegment(sketch, "E28.0.2.69", {"start": v(30.2, 57.8) * mm, "end": v(30.2, 47.8) * mm});
            skLineSegment(sketch, "E28.0.2.70", {"start": v(2.2, 62.8) * mm, "end": v(2.2, 72.8) * mm});
            skLineSegment(sketch, "E28.0.2.71", {"start": v(-62.6, 57.8) * mm, "end": v(-43.3, 57.8) * mm});
            skLineSegment(sketch, "E28.0.2.72", {"start": v(-67, 47.8) * mm, "end": v(-86.3, 47.8) * mm});
            skLineSegment(sketch, "E28.0.2.73", {"start": v(67, 32.8) * mm, "end": v(67, 42.8) * mm});
            skLineSegment(sketch, "E28.0.2.74", {"start": v(-95, 32.8) * mm, "end": v(-95, 42.8) * mm});
            skLineSegment(sketch, "E28.0.2.75", {"start": v(62.6, 72.8) * mm, "end": v(62.6, 62.8) * mm});
            skLineSegment(sketch, "E28.0.2.76", {"start": v(67, 72.8) * mm, "end": v(86.3, 72.8) * mm});
            skLineSegment(sketch, "E28.0.2.77", {"start": v(-43.3, 72.8) * mm, "end": v(-62.6, 62.8) * mm});
            skLineSegment(sketch, "E28.0.2.78", {"start": v(95, 62.8) * mm, "end": v(75.7, 62.8) * mm});
            skLineSegment(sketch, "E28.0.2.79", {"start": v(30.2, 32.8) * mm, "end": v(10.9, 32.8) * mm});
            skLineSegment(sketch, "E28.0.2.80", {"start": v(-86.3, 32.8) * mm, "end": v(-67, 42.8) * mm});
            skLineSegment(sketch, "E28.0.2.81", {"start": v(-2.2, 32.8) * mm, "end": v(-21.5, 32.8) * mm});
            skLineSegment(sketch, "E28.0.2.82", {"start": v(62.6, 32.8) * mm, "end": v(43.3, 32.8) * mm});
            skLineSegment(sketch, "E28.0.2.83", {"start": v(-34.6, 72.8) * mm, "end": v(-34.6, 62.8) * mm});
            skLineSegment(sketch, "E28.0.2.84", {"start": v(53.9, 57.8) * mm, "end": v(34.6, 47.8) * mm});
            skLineSegment(sketch, "E28.0.2.85", {"start": v(-53.9, 47.8) * mm, "end": v(-34.6, 57.8) * mm});
            skLineSegment(sketch, "E28.0.2.86", {"start": v(75.7, 62.8) * mm, "end": v(95, 72.8) * mm});
            skLineSegment(sketch, "E28.0.2.87", {"start": v(67, 47.8) * mm, "end": v(67, 57.8) * mm});
            skLineSegment(sketch, "E28.0.2.88", {"start": v(2.2, 32.8) * mm, "end": v(2.2, 42.8) * mm});
            skLineSegment(sketch, "E28.0.2.89", {"start": v(-2.2, 72.8) * mm, "end": v(-2.2, 62.8) * mm});
            skLineSegment(sketch, "E28.0.2.90", {"start": v(30.2, 42.8) * mm, "end": v(30.2, 32.8) * mm});
            skLineSegment(sketch, "E28.0.2.91", {"start": v(95, 32.8) * mm, "end": v(75.7, 32.8) * mm});
            skLineSegment(sketch, "E28.0.2.92", {"start": v(-95, 62.8) * mm, "end": v(-95, 47.8) * mm, "construction": true});
            skLineSegment(sketch, "E28.0.2.93", {"start": v(-53.9, 62.8) * mm, "end": v(-34.6, 72.8) * mm});
            skLineSegment(sketch, "E28.0.2.94", {"start": v(-21.5, 62.8) * mm, "end": v(-2.2, 72.8) * mm});
            skLineSegment(sketch, "E28.0.2.95", {"start": v(-62.6, 62.8) * mm, "end": v(-62.6, 72.8) * mm});
            skLineSegment(sketch, "E28.0.2.96", {"start": v(21.5, 42.8) * mm, "end": v(2.2, 32.8) * mm});
            skLineSegment(sketch, "E28.0.2.97", {"start": v(-53.9, 32.8) * mm, "end": v(-34.6, 42.8) * mm});
            skLineSegment(sketch, "E28.0.2.98", {"start": v(2.2, 57.8) * mm, "end": v(21.5, 57.8) * mm});
            skLineSegment(sketch, "E28.0.2.99", {"start": v(62.6, 42.8) * mm, "end": v(62.6, 32.8) * mm});
            skLineSegment(sketch, "E28.0.2.100", {"start": v(-67, 32.8) * mm, "end": v(-86.3, 32.8) * mm});
            skLineSegment(sketch, "E28.0.2.101", {"start": v(53.9, 72.8) * mm, "end": v(34.6, 62.8) * mm});
            skLineSegment(sketch, "E28.0.2.102", {"start": v(-21.5, 47.8) * mm, "end": v(-2.2, 57.8) * mm});
            skLineSegment(sketch, "E28.0.2.103", {"start": v(95, 72.8) * mm, "end": v(95, 62.8) * mm});
            skLineSegment(sketch, "E28.0.2.104", {"start": v(-62.6, 32.8) * mm, "end": v(-62.6, 42.8) * mm});
            skLineSegment(sketch, "E28.0.2.105", {"start": v(75.7, 32.8) * mm, "end": v(95, 42.8) * mm});
            skLineSegment(sketch, "E28.0.2.106", {"start": v(10.9, 62.8) * mm, "end": v(30.2, 72.8) * mm});
            skLineSegment(sketch, "E28.0.2.107", {"start": v(-2.2, 57.8) * mm, "end": v(-2.2, 47.8) * mm});
            skLineSegment(sketch, "E28.0.2.108", {"start": v(-67, 62.8) * mm, "end": v(-86.3, 62.8) * mm});
            skLineSegment(sketch, "E28.0.2.109", {"start": v(-95, 47.8) * mm, "end": v(-95, 57.8) * mm});
            skLineSegment(sketch, "E28.direction1", {"start": v(-95, 132.8) * mm, "end": v(-70, 132.8) * mm, "construction": true});
            skLineSegment(sketch, "E28.direction2", {"start": v(-95, 132.8) * mm, "end": v(-95, 82.8) * mm, "construction": true});
            skSolve(sketch);
        }
        {
            var Q0;
            Q0=makeQuery(id+"F3.imprint","IMPRINT",FACE,{"disambiguationData":[TD([[makeQuery(id+"F3.imprint","IMPRINT",EDGE,{"derivedFrom":sQuery(id+"F3.wireOp",EDGE,"E21")}),-1.0]])]});
            var Q1;
            Q1=makeQuery(id+"F3.imprint","IMPRINT",FACE,{"disambiguationData":[TD([[makeQuery(id+"F3.imprint","IMPRINT",EDGE,{"derivedFrom":sQuery(id+"F3.wireOp",EDGE,"E24")}),-1.0]])]});
            var Q2;
            Q2=makeQuery(id+"F3.imprint","IMPRINT",FACE,{"disambiguationData":[TD([[makeQuery(id+"F3.imprint","IMPRINT",EDGE,{"derivedFrom":sQuery(id+"F3.wireOp",EDGE,"f00be4c2-0bb6-4201-85ea-d6b214965bce.1.0.2")}),-1.0]])]});
            var Q3;
            Q3=makeQuery(id+"F3.imprint","IMPRINT",FACE,{"disambiguationData":[TD([[makeQuery(id+"F3.imprint","IMPRINT",EDGE,{"derivedFrom":sQuery(id+"F3.wireOp",EDGE,"f00be4c2-0bb6-4201-85ea-d6b214965bce.1.0.0")}),-1.0]])]});
            var Q4;
            Q4=makeQuery(id+"F3.imprint","IMPRINT",FACE,{"disambiguationData":[TD([[makeQuery(id+"F3.imprint","IMPRINT",EDGE,{"derivedFrom":sQuery(id+"F3.wireOp",EDGE,"f00be4c2-0bb6-4201-85ea-d6b214965bce.2.0.2")}),-1.0]])]});
            var Q5;
            Q5=makeQuery(id+"F3.imprint","IMPRINT",FACE,{"disambiguationData":[TD([[makeQuery(id+"F3.imprint","IMPRINT",EDGE,{"derivedFrom":sQuery(id+"F3.wireOp",EDGE,"f00be4c2-0bb6-4201-85ea-d6b214965bce.2.0.0")}),-1.0]])]});
            var Q6;
            Q6=makeQuery(id+"F3.imprint","IMPRINT",FACE,{"disambiguationData":[TD([[makeQuery(id+"F3.imprint","IMPRINT",EDGE,{"derivedFrom":sQuery(id+"F3.wireOp",EDGE,"956dcd40-a7e3-4733-8d9c-644aff1a401c.0.1.0")}),-1.0]])]});
            var Q7;
            Q7=makeQuery(id+"F3.imprint","IMPRINT",FACE,{"disambiguationData":[TD([[makeQuery(id+"F3.imprint","IMPRINT",EDGE,{"derivedFrom":sQuery(id+"F3.wireOp",EDGE,"956dcd40-a7e3-4733-8d9c-644aff1a401c.0.1.9")}),-1.0]])]});
            var Q8;
            Q8=makeQuery(id+"F3.imprint","IMPRINT",FACE,{"disambiguationData":[TD([[makeQuery(id+"F3.imprint","IMPRINT",EDGE,{"derivedFrom":sQuery(id+"F3.wireOp",EDGE,"956dcd40-a7e3-4733-8d9c-644aff1a401c.0.2.0")}),-1.0]])]});
            var Q9;
            Q9=makeQuery(id+"F3.imprint","IMPRINT",FACE,{"disambiguationData":[TD([[makeQuery(id+"F3.imprint","IMPRINT",EDGE,{"derivedFrom":sQuery(id+"F3.wireOp",EDGE,"956dcd40-a7e3-4733-8d9c-644aff1a401c.0.2.9")}),-1.0]])]});
            var Q10;
            Q10=makeQuery(id+"F3.imprint","IMPRINT",FACE,{"disambiguationData":[TD([[makeQuery(id+"F3.imprint","IMPRINT",EDGE,{"derivedFrom":sQuery(id+"F3.wireOp",EDGE,"956dcd40-a7e3-4733-8d9c-644aff1a401c.0.2.1")}),-1.0]])]});
            var Q11;
            Q11=makeQuery(id+"F3.imprint","IMPRINT",FACE,{"disambiguationData":[TD([[makeQuery(id+"F3.imprint","IMPRINT",EDGE,{"derivedFrom":sQuery(id+"F3.wireOp",EDGE,"956dcd40-a7e3-4733-8d9c-644aff1a401c.0.2.11")}),-1.0]])]});
            var Q12;
            Q12=makeQuery(id+"F3.imprint","IMPRINT",FACE,{"disambiguationData":[TD([[makeQuery(id+"F3.imprint","IMPRINT",EDGE,{"derivedFrom":sQuery(id+"F3.wireOp",EDGE,"956dcd40-a7e3-4733-8d9c-644aff1a401c.0.2.3")}),-1.0]])]});
            var Q13;
            Q13=makeQuery(id+"F3.imprint","IMPRINT",FACE,{"disambiguationData":[TD([[makeQuery(id+"F3.imprint","IMPRINT",EDGE,{"derivedFrom":sQuery(id+"F3.wireOp",EDGE,"956dcd40-a7e3-4733-8d9c-644aff1a401c.0.2.2")}),-1.0]])]});
            var Q14;
            Q14=makeQuery(id+"F3.imprint","IMPRINT",FACE,{"disambiguationData":[TD([[makeQuery(id+"F3.imprint","IMPRINT",EDGE,{"derivedFrom":sQuery(id+"F3.wireOp",EDGE,"956dcd40-a7e3-4733-8d9c-644aff1a401c.0.1.2")}),-1.0]])]});
            var Q15;
            Q15=makeQuery(id+"F3.imprint","IMPRINT",FACE,{"disambiguationData":[TD([[makeQuery(id+"F3.imprint","IMPRINT",EDGE,{"derivedFrom":sQuery(id+"F3.wireOp",EDGE,"956dcd40-a7e3-4733-8d9c-644aff1a401c.0.1.3")}),-1.0]])]});
            var Q16;
            Q16=makeQuery(id+"F3.imprint","IMPRINT",FACE,{"disambiguationData":[TD([[makeQuery(id+"F3.imprint","IMPRINT",EDGE,{"derivedFrom":sQuery(id+"F3.wireOp",EDGE,"956dcd40-a7e3-4733-8d9c-644aff1a401c.0.1.11")}),-1.0]])]});
            var Q17;
            Q17=makeQuery(id+"F3.imprint","IMPRINT",FACE,{"disambiguationData":[TD([[makeQuery(id+"F3.imprint","IMPRINT",EDGE,{"derivedFrom":sQuery(id+"F3.wireOp",EDGE,"956dcd40-a7e3-4733-8d9c-644aff1a401c.0.1.1")}),-1.0]])]});
            var Q18;
            Q18=makeQuery(id+"F3.imprint","IMPRINT",FACE,{"disambiguationData":[TD([[makeQuery(id+"F3.imprint","IMPRINT",EDGE,{"derivedFrom":sQuery(id+"F3.wireOp",EDGE,"E27.1.0.2")}),-1.0]])]});
            var Q19;
            Q19=makeQuery(id+"F3.imprint","IMPRINT",FACE,{"disambiguationData":[TD([[makeQuery(id+"F3.imprint","IMPRINT",EDGE,{"derivedFrom":sQuery(id+"F3.wireOp",EDGE,"E27.1.0.0")}),-1.0]])]});
            var Q20;
            Q20=makeQuery(id+"F3.imprint","IMPRINT",FACE,{"disambiguationData":[TD([[makeQuery(id+"F3.imprint","IMPRINT",EDGE,{"derivedFrom":sQuery(id+"F3.wireOp",EDGE,"E27.2.0.2")}),-1.0]])]});
            var Q21;
            Q21=makeQuery(id+"F3.imprint","IMPRINT",FACE,{"disambiguationData":[TD([[makeQuery(id+"F3.imprint","IMPRINT",EDGE,{"derivedFrom":sQuery(id+"F3.wireOp",EDGE,"E27.2.0.0")}),-1.0]])]});
            var Q22;
            Q22=makeQuery(id+"F3.imprint","IMPRINT",FACE,{"disambiguationData":[TD([[makeQuery(id+"F3.imprint","IMPRINT",EDGE,{"derivedFrom":sQuery(id+"F3.wireOp",EDGE,"E27.3.0.2")}),-1.0]])]});
            var Q23;
            Q23=makeQuery(id+"F3.imprint","IMPRINT",FACE,{"disambiguationData":[TD([[makeQuery(id+"F3.imprint","IMPRINT",EDGE,{"derivedFrom":sQuery(id+"F3.wireOp",EDGE,"E27.3.0.0")}),-1.0]])]});
            var Q24;
            Q24=makeQuery(id+"F3.imprint","IMPRINT",FACE,{"disambiguationData":[TD([[makeQuery(id+"F3.imprint","IMPRINT",EDGE,{"derivedFrom":sQuery(id+"F3.wireOp",EDGE,"E27.4.0.2")}),-1.0]])]});
            var Q25;
            Q25=makeQuery(id+"F3.imprint","IMPRINT",FACE,{"disambiguationData":[TD([[makeQuery(id+"F3.imprint","IMPRINT",EDGE,{"derivedFrom":sQuery(id+"F3.wireOp",EDGE,"E27.4.0.0")}),-1.0]])]});
            var Q26;
            Q26=makeQuery(id+"F3.imprint","IMPRINT",FACE,{"disambiguationData":[TD([[makeQuery(id+"F3.imprint","IMPRINT",EDGE,{"derivedFrom":sQuery(id+"F3.wireOp",EDGE,"E27.5.0.2")}),-1.0]])]});
            var Q27;
            Q27=makeQuery(id+"F3.imprint","IMPRINT",FACE,{"disambiguationData":[TD([[makeQuery(id+"F3.imprint","IMPRINT",EDGE,{"derivedFrom":sQuery(id+"F3.wireOp",EDGE,"E27.5.0.0")}),-1.0]])]});
            var Q28;
            Q28=makeQuery(id+"F3.imprint","IMPRINT",FACE,{"disambiguationData":[TD([[makeQuery(id+"F3.imprint","IMPRINT",EDGE,{"derivedFrom":sQuery(id+"F3.wireOp",EDGE,"E27.5.1.2")}),-1.0]])]});
            var Q29;
            Q29=makeQuery(id+"F3.imprint","IMPRINT",FACE,{"disambiguationData":[TD([[makeQuery(id+"F3.imprint","IMPRINT",EDGE,{"derivedFrom":sQuery(id+"F3.wireOp",EDGE,"E27.5.1.0")}),-1.0]])]});
            var Q30;
            Q30=makeQuery(id+"F3.imprint","IMPRINT",FACE,{"disambiguationData":[TD([[makeQuery(id+"F3.imprint","IMPRINT",EDGE,{"derivedFrom":sQuery(id+"F3.wireOp",EDGE,"E27.5.2.2")}),-1.0]])]});
            var Q31;
            Q31=makeQuery(id+"F3.imprint","IMPRINT",FACE,{"disambiguationData":[TD([[makeQuery(id+"F3.imprint","IMPRINT",EDGE,{"derivedFrom":sQuery(id+"F3.wireOp",EDGE,"E27.5.2.0")}),-1.0]])]});
            var Q32;
            Q32=makeQuery(id+"F3.imprint","IMPRINT",FACE,{"disambiguationData":[TD([[makeQuery(id+"F3.imprint","IMPRINT",EDGE,{"derivedFrom":sQuery(id+"F3.wireOp",EDGE,"E27.4.2.0")}),-1.0]])]});
            var Q33;
            Q33=makeQuery(id+"F3.imprint","IMPRINT",FACE,{"disambiguationData":[TD([[makeQuery(id+"F3.imprint","IMPRINT",EDGE,{"derivedFrom":sQuery(id+"F3.wireOp",EDGE,"E27.4.2.2")}),-1.0]])]});
            var Q34;
            Q34=makeQuery(id+"F3.imprint","IMPRINT",FACE,{"disambiguationData":[TD([[makeQuery(id+"F3.imprint","IMPRINT",EDGE,{"derivedFrom":sQuery(id+"F3.wireOp",EDGE,"E27.3.2.0")}),-1.0]])]});
            var Q35;
            Q35=makeQuery(id+"F3.imprint","IMPRINT",FACE,{"disambiguationData":[TD([[makeQuery(id+"F3.imprint","IMPRINT",EDGE,{"derivedFrom":sQuery(id+"F3.wireOp",EDGE,"E27.3.2.2")}),-1.0]])]});
            var Q36;
            Q36=makeQuery(id+"F3.imprint","IMPRINT",FACE,{"disambiguationData":[TD([[makeQuery(id+"F3.imprint","IMPRINT",EDGE,{"derivedFrom":sQuery(id+"F3.wireOp",EDGE,"E27.2.2.0")}),-1.0]])]});
            var Q37;
            Q37=makeQuery(id+"F3.imprint","IMPRINT",FACE,{"disambiguationData":[TD([[makeQuery(id+"F3.imprint","IMPRINT",EDGE,{"derivedFrom":sQuery(id+"F3.wireOp",EDGE,"E27.2.2.2")}),-1.0]])]});
            var Q38;
            Q38=makeQuery(id+"F3.imprint","IMPRINT",FACE,{"disambiguationData":[TD([[makeQuery(id+"F3.imprint","IMPRINT",EDGE,{"derivedFrom":sQuery(id+"F3.wireOp",EDGE,"E27.1.2.0")}),-1.0]])]});
            var Q39;
            Q39=makeQuery(id+"F3.imprint","IMPRINT",FACE,{"disambiguationData":[TD([[makeQuery(id+"F3.imprint","IMPRINT",EDGE,{"derivedFrom":sQuery(id+"F3.wireOp",EDGE,"E27.1.2.2")}),-1.0]])]});
            var Q40;
            Q40=makeQuery(id+"F3.imprint","IMPRINT",FACE,{"disambiguationData":[TD([[makeQuery(id+"F3.imprint","IMPRINT",EDGE,{"derivedFrom":sQuery(id+"F3.wireOp",EDGE,"E27.0.2.0")}),-1.0]])]});
            var Q41;
            Q41=makeQuery(id+"F3.imprint","IMPRINT",FACE,{"disambiguationData":[TD([[makeQuery(id+"F3.imprint","IMPRINT",EDGE,{"derivedFrom":sQuery(id+"F3.wireOp",EDGE,"E27.0.2.2")}),-1.0]])]});
            var Q42;
            Q42=makeQuery(id+"F3.imprint","IMPRINT",FACE,{"disambiguationData":[TD([[makeQuery(id+"F3.imprint","IMPRINT",EDGE,{"derivedFrom":sQuery(id+"F3.wireOp",EDGE,"E27.0.1.2")}),-1.0]])]});
            var Q43;
            Q43=makeQuery(id+"F3.imprint","IMPRINT",FACE,{"disambiguationData":[TD([[makeQuery(id+"F3.imprint","IMPRINT",EDGE,{"derivedFrom":sQuery(id+"F3.wireOp",EDGE,"E27.0.1.0")}),-1.0]])]});
            var Q44;
            Q44=makeQuery(id+"F3.imprint","IMPRINT",FACE,{"disambiguationData":[TD([[makeQuery(id+"F3.imprint","IMPRINT",EDGE,{"derivedFrom":sQuery(id+"F3.wireOp",EDGE,"E27.1.1.2")}),-1.0]])]});
            var Q45;
            Q45=makeQuery(id+"F3.imprint","IMPRINT",FACE,{"disambiguationData":[TD([[makeQuery(id+"F3.imprint","IMPRINT",EDGE,{"derivedFrom":sQuery(id+"F3.wireOp",EDGE,"E27.1.1.0")}),-1.0]])]});
            var Q46;
            Q46=makeQuery(id+"F3.imprint","IMPRINT",FACE,{"disambiguationData":[TD([[makeQuery(id+"F3.imprint","IMPRINT",EDGE,{"derivedFrom":sQuery(id+"F3.wireOp",EDGE,"E27.2.1.2")}),-1.0]])]});
            var Q47;
            Q47=makeQuery(id+"F3.imprint","IMPRINT",FACE,{"disambiguationData":[TD([[makeQuery(id+"F3.imprint","IMPRINT",EDGE,{"derivedFrom":sQuery(id+"F3.wireOp",EDGE,"E27.2.1.0")}),-1.0]])]});
            var Q48;
            Q48=makeQuery(id+"F3.imprint","IMPRINT",FACE,{"disambiguationData":[TD([[makeQuery(id+"F3.imprint","IMPRINT",EDGE,{"derivedFrom":sQuery(id+"F3.wireOp",EDGE,"E27.3.1.2")}),-1.0]])]});
            var Q49;
            Q49=makeQuery(id+"F3.imprint","IMPRINT",FACE,{"disambiguationData":[TD([[makeQuery(id+"F3.imprint","IMPRINT",EDGE,{"derivedFrom":sQuery(id+"F3.wireOp",EDGE,"E27.3.1.0")}),-1.0]])]});
            var Q50;
            Q50=makeQuery(id+"F3.imprint","IMPRINT",FACE,{"disambiguationData":[TD([[makeQuery(id+"F3.imprint","IMPRINT",EDGE,{"derivedFrom":sQuery(id+"F3.wireOp",EDGE,"E27.4.1.2")}),-1.0]])]});
            var Q51;
            Q51=makeQuery(id+"F3.imprint","IMPRINT",FACE,{"disambiguationData":[TD([[makeQuery(id+"F3.imprint","IMPRINT",EDGE,{"derivedFrom":sQuery(id+"F3.wireOp",EDGE,"E27.4.1.0")}),-1.0]])]});
            var Q52;
            Q52=makeQuery(id+"F3.imprint","IMPRINT",FACE,{"disambiguationData":[TD([[makeQuery(id+"F3.imprint","IMPRINT",EDGE,{"derivedFrom":sQuery(id+"F3.wireOp",EDGE,"E28.0.1.6")}),-1.0]])]});
            var Q53;
            Q53=makeQuery(id+"F3.imprint","IMPRINT",FACE,{"disambiguationData":[TD([[makeQuery(id+"F3.imprint","IMPRINT",EDGE,{"derivedFrom":sQuery(id+"F3.wireOp",EDGE,"E28.0.1.9")}),-1.0]])]});
            var Q54;
            Q54=makeQuery(id+"F3.imprint","IMPRINT",FACE,{"disambiguationData":[TD([[makeQuery(id+"F3.imprint","IMPRINT",EDGE,{"derivedFrom":sQuery(id+"F3.wireOp",EDGE,"E28.0.1.5")}),-1.0]])]});
            var Q55;
            Q55=makeQuery(id+"F3.imprint","IMPRINT",FACE,{"disambiguationData":[TD([[makeQuery(id+"F3.imprint","IMPRINT",EDGE,{"derivedFrom":sQuery(id+"F3.wireOp",EDGE,"E28.0.1.26")}),-1.0]])]});
            var Q56;
            Q56=makeQuery(id+"F3.imprint","IMPRINT",FACE,{"disambiguationData":[TD([[makeQuery(id+"F3.imprint","IMPRINT",EDGE,{"derivedFrom":sQuery(id+"F3.wireOp",EDGE,"E28.0.1.29")}),-1.0]])]});
            var Q57;
            Q57=makeQuery(id+"F3.imprint","IMPRINT",FACE,{"disambiguationData":[TD([[makeQuery(id+"F3.imprint","IMPRINT",EDGE,{"derivedFrom":sQuery(id+"F3.wireOp",EDGE,"E28.0.1.44")}),-1.0]])]});
            var Q58;
            Q58=makeQuery(id+"F3.imprint","IMPRINT",FACE,{"disambiguationData":[TD([[makeQuery(id+"F3.imprint","IMPRINT",EDGE,{"derivedFrom":sQuery(id+"F3.wireOp",EDGE,"E28.0.1.36")}),-1.0]])]});
            var Q59;
            Q59=makeQuery(id+"F3.imprint","IMPRINT",FACE,{"disambiguationData":[TD([[makeQuery(id+"F3.imprint","IMPRINT",EDGE,{"derivedFrom":sQuery(id+"F3.wireOp",EDGE,"E28.0.1.1")}),-1.0]])]});
            var Q60;
            Q60=makeQuery(id+"F3.imprint","IMPRINT",FACE,{"disambiguationData":[TD([[makeQuery(id+"F3.imprint","IMPRINT",EDGE,{"derivedFrom":sQuery(id+"F3.wireOp",EDGE,"E28.0.1.2")}),-1.0]])]});
            var Q61;
            Q61=makeQuery(id+"F3.imprint","IMPRINT",FACE,{"disambiguationData":[TD([[makeQuery(id+"F3.imprint","IMPRINT",EDGE,{"derivedFrom":sQuery(id+"F3.wireOp",EDGE,"E28.0.1.8")}),-1.0]])]});
            var Q62;
            Q62=makeQuery(id+"F3.imprint","IMPRINT",FACE,{"disambiguationData":[TD([[makeQuery(id+"F3.imprint","IMPRINT",EDGE,{"derivedFrom":sQuery(id+"F3.wireOp",EDGE,"E28.0.1.28")}),-1.0]])]});
            var Q63;
            Q63=makeQuery(id+"F3.imprint","IMPRINT",FACE,{"disambiguationData":[TD([[makeQuery(id+"F3.imprint","IMPRINT",EDGE,{"derivedFrom":sQuery(id+"F3.wireOp",EDGE,"E28.0.1.60")}),-1.0]])]});
            var Q64;
            Q64=makeQuery(id+"F3.imprint","IMPRINT",FACE,{"disambiguationData":[TD([[makeQuery(id+"F3.imprint","IMPRINT",EDGE,{"derivedFrom":sQuery(id+"F3.wireOp",EDGE,"E28.0.1.3")}),-1.0]])]});
            var Q65;
            Q65=makeQuery(id+"F3.imprint","IMPRINT",FACE,{"disambiguationData":[TD([[makeQuery(id+"F3.imprint","IMPRINT",EDGE,{"derivedFrom":sQuery(id+"F3.wireOp",EDGE,"E28.0.1.34")}),-1.0]])]});
            var Q66;
            Q66=makeQuery(id+"F3.imprint","IMPRINT",FACE,{"disambiguationData":[TD([[makeQuery(id+"F3.imprint","IMPRINT",EDGE,{"derivedFrom":sQuery(id+"F3.wireOp",EDGE,"E28.0.1.47")}),-1.0]])]});
            var Q67;
            Q67=makeQuery(id+"F3.imprint","IMPRINT",FACE,{"disambiguationData":[TD([[makeQuery(id+"F3.imprint","IMPRINT",EDGE,{"derivedFrom":sQuery(id+"F3.wireOp",EDGE,"E28.0.1.57")}),-1.0]])]});
            var Q68;
            Q68=makeQuery(id+"F3.imprint","IMPRINT",FACE,{"disambiguationData":[TD([[makeQuery(id+"F3.imprint","IMPRINT",EDGE,{"derivedFrom":sQuery(id+"F3.wireOp",EDGE,"E28.0.1.20")}),-1.0]])]});
            var Q69;
            Q69=makeQuery(id+"F3.imprint","IMPRINT",FACE,{"disambiguationData":[TD([[makeQuery(id+"F3.imprint","IMPRINT",EDGE,{"derivedFrom":sQuery(id+"F3.wireOp",EDGE,"E28.0.1.24")}),-1.0]])]});
            var Q70;
            Q70=makeQuery(id+"F3.imprint","IMPRINT",FACE,{"disambiguationData":[TD([[makeQuery(id+"F3.imprint","IMPRINT",EDGE,{"derivedFrom":sQuery(id+"F3.wireOp",EDGE,"E28.0.1.22")}),-1.0]])]});
            var Q71;
            Q71=makeQuery(id+"F3.imprint","IMPRINT",FACE,{"disambiguationData":[TD([[makeQuery(id+"F3.imprint","IMPRINT",EDGE,{"derivedFrom":sQuery(id+"F3.wireOp",EDGE,"E28.0.1.52")}),-1.0]])]});
            var Q72;
            Q72=makeQuery(id+"F3.imprint","IMPRINT",FACE,{"disambiguationData":[TD([[makeQuery(id+"F3.imprint","IMPRINT",EDGE,{"derivedFrom":sQuery(id+"F3.wireOp",EDGE,"E28.0.1.23")}),-1.0]])]});
            var Q73;
            Q73=makeQuery(id+"F3.imprint","IMPRINT",FACE,{"disambiguationData":[TD([[makeQuery(id+"F3.imprint","IMPRINT",EDGE,{"derivedFrom":sQuery(id+"F3.wireOp",EDGE,"E28.0.1.15")}),-1.0]])]});
            var Q74;
            Q74=makeQuery(id+"F3.imprint","IMPRINT",FACE,{"disambiguationData":[TD([[makeQuery(id+"F3.imprint","IMPRINT",EDGE,{"derivedFrom":sQuery(id+"F3.wireOp",EDGE,"E28.0.1.4")}),-1.0]])]});
            var Q75;
            Q75=makeQuery(id+"F3.imprint","IMPRINT",FACE,{"disambiguationData":[TD([[makeQuery(id+"F3.imprint","IMPRINT",EDGE,{"derivedFrom":sQuery(id+"F3.wireOp",EDGE,"E28.0.1.32")}),-1.0]])]});
            var Q76;
            Q76=makeQuery(id+"F3.imprint","IMPRINT",FACE,{"disambiguationData":[TD([[makeQuery(id+"F3.imprint","IMPRINT",EDGE,{"derivedFrom":sQuery(id+"F3.wireOp",EDGE,"E28.0.1.10")}),-1.0]])]});
            var Q77;
            Q77=makeQuery(id+"F3.imprint","IMPRINT",FACE,{"disambiguationData":[TD([[makeQuery(id+"F3.imprint","IMPRINT",EDGE,{"derivedFrom":sQuery(id+"F3.wireOp",EDGE,"E28.0.1.11")}),-1.0]])]});
            var Q78;
            Q78=makeQuery(id+"F3.imprint","IMPRINT",FACE,{"disambiguationData":[TD([[makeQuery(id+"F3.imprint","IMPRINT",EDGE,{"derivedFrom":sQuery(id+"F3.wireOp",EDGE,"E28.0.1.49")}),-1.0]])]});
            var Q79;
            Q79=makeQuery(id+"F3.imprint","IMPRINT",FACE,{"disambiguationData":[TD([[makeQuery(id+"F3.imprint","IMPRINT",EDGE,{"derivedFrom":sQuery(id+"F3.wireOp",EDGE,"E28.0.1.51")}),-1.0]])]});
            var Q80;
            Q80=makeQuery(id+"F3.imprint","IMPRINT",FACE,{"disambiguationData":[TD([[makeQuery(id+"F3.imprint","IMPRINT",EDGE,{"derivedFrom":sQuery(id+"F3.wireOp",EDGE,"E28.0.1.17")}),-1.0]])]});
            var Q81;
            Q81=makeQuery(id+"F3.imprint","IMPRINT",FACE,{"disambiguationData":[TD([[makeQuery(id+"F3.imprint","IMPRINT",EDGE,{"derivedFrom":sQuery(id+"F3.wireOp",EDGE,"E28.0.1.21")}),-1.0]])]});
            var Q82;
            Q82=makeQuery(id+"F3.imprint","IMPRINT",FACE,{"disambiguationData":[TD([[makeQuery(id+"F3.imprint","IMPRINT",EDGE,{"derivedFrom":sQuery(id+"F3.wireOp",EDGE,"E28.0.1.38")}),-1.0]])]});
            var Q83;
            Q83=makeQuery(id+"F3.imprint","IMPRINT",FACE,{"disambiguationData":[TD([[makeQuery(id+"F3.imprint","IMPRINT",EDGE,{"derivedFrom":sQuery(id+"F3.wireOp",EDGE,"E28.0.1.7")}),-1.0]])]});
            var Q84;
            Q84=makeQuery(id+"F3.imprint","IMPRINT",FACE,{"disambiguationData":[TD([[makeQuery(id+"F3.imprint","IMPRINT",EDGE,{"derivedFrom":sQuery(id+"F3.wireOp",EDGE,"E28.0.1.0")}),-1.0]])]});
            var Q85;
            Q85=makeQuery(id+"F3.imprint","IMPRINT",FACE,{"disambiguationData":[TD([[makeQuery(id+"F3.imprint","IMPRINT",EDGE,{"derivedFrom":sQuery(id+"F3.wireOp",EDGE,"E28.0.1.12")}),-1.0]])]});
            var Q86;
            Q86=makeQuery(id+"F3.imprint","IMPRINT",FACE,{"disambiguationData":[TD([[makeQuery(id+"F3.imprint","IMPRINT",EDGE,{"derivedFrom":sQuery(id+"F3.wireOp",EDGE,"E28.0.1.37")}),-1.0]])]});
            var Q87;
            Q87=makeQuery(id+"F3.imprint","IMPRINT",FACE,{"disambiguationData":[TD([[makeQuery(id+"F3.imprint","IMPRINT",EDGE,{"derivedFrom":sQuery(id+"F3.wireOp",EDGE,"E28.0.1.78")}),-1.0]])]});
            var Q88;
            Q88=makeQuery(id+"F3.imprint","IMPRINT",FACE,{"disambiguationData":[TD([[makeQuery(id+"F3.imprint","IMPRINT",EDGE,{"derivedFrom":sQuery(id+"F3.wireOp",EDGE,"E28.0.2.6")}),-1.0]])]});
            var Q89;
            Q89=makeQuery(id+"F3.imprint","IMPRINT",FACE,{"disambiguationData":[TD([[makeQuery(id+"F3.imprint","IMPRINT",EDGE,{"derivedFrom":sQuery(id+"F3.wireOp",EDGE,"E28.0.2.5")}),-1.0]])]});
            var Q90;
            Q90=makeQuery(id+"F3.imprint","IMPRINT",FACE,{"disambiguationData":[TD([[makeQuery(id+"F3.imprint","IMPRINT",EDGE,{"derivedFrom":sQuery(id+"F3.wireOp",EDGE,"E28.0.2.26")}),-1.0]])]});
            var Q91;
            Q91=makeQuery(id+"F3.imprint","IMPRINT",FACE,{"disambiguationData":[TD([[makeQuery(id+"F3.imprint","IMPRINT",EDGE,{"derivedFrom":sQuery(id+"F3.wireOp",EDGE,"E28.0.2.44")}),-1.0]])]});
            var Q92;
            Q92=makeQuery(id+"F3.imprint","IMPRINT",FACE,{"disambiguationData":[TD([[makeQuery(id+"F3.imprint","IMPRINT",EDGE,{"derivedFrom":sQuery(id+"F3.wireOp",EDGE,"E28.0.2.29")}),-1.0]])]});
            var Q93;
            Q93=makeQuery(id+"F3.imprint","IMPRINT",FACE,{"disambiguationData":[TD([[makeQuery(id+"F3.imprint","IMPRINT",EDGE,{"derivedFrom":sQuery(id+"F3.wireOp",EDGE,"E28.0.2.9")}),-1.0]])]});
            var Q94;
            Q94=makeQuery(id+"F3.imprint","IMPRINT",FACE,{"disambiguationData":[TD([[makeQuery(id+"F3.imprint","IMPRINT",EDGE,{"derivedFrom":sQuery(id+"F3.wireOp",EDGE,"E28.0.2.49")}),-1.0]])]});
            var Q95;
            Q95=makeQuery(id+"F3.imprint","IMPRINT",FACE,{"disambiguationData":[TD([[makeQuery(id+"F3.imprint","IMPRINT",EDGE,{"derivedFrom":sQuery(id+"F3.wireOp",EDGE,"E28.0.2.51")}),-1.0]])]});
            var Q96;
            Q96=makeQuery(id+"F3.imprint","IMPRINT",FACE,{"disambiguationData":[TD([[makeQuery(id+"F3.imprint","IMPRINT",EDGE,{"derivedFrom":sQuery(id+"F3.wireOp",EDGE,"E28.0.2.11")}),-1.0]])]});
            var Q97;
            Q97=makeQuery(id+"F3.imprint","IMPRINT",FACE,{"disambiguationData":[TD([[makeQuery(id+"F3.imprint","IMPRINT",EDGE,{"derivedFrom":sQuery(id+"F3.wireOp",EDGE,"E28.0.2.10")}),-1.0]])]});
            var Q98;
            Q98=makeQuery(id+"F3.imprint","IMPRINT",FACE,{"disambiguationData":[TD([[makeQuery(id+"F3.imprint","IMPRINT",EDGE,{"derivedFrom":sQuery(id+"F3.wireOp",EDGE,"E28.0.2.36")}),-1.0]])]});
            var Q99;
            Q99=makeQuery(id+"F3.imprint","IMPRINT",FACE,{"disambiguationData":[TD([[makeQuery(id+"F3.imprint","IMPRINT",EDGE,{"derivedFrom":sQuery(id+"F3.wireOp",EDGE,"E28.0.2.1")}),-1.0]])]});
            var Q100;
            Q100=makeQuery(id+"F3.imprint","IMPRINT",FACE,{"disambiguationData":[TD([[makeQuery(id+"F3.imprint","IMPRINT",EDGE,{"derivedFrom":sQuery(id+"F3.wireOp",EDGE,"E28.0.2.2")}),-1.0]])]});
            var Q101;
            Q101=makeQuery(id+"F3.imprint","IMPRINT",FACE,{"disambiguationData":[TD([[makeQuery(id+"F3.imprint","IMPRINT",EDGE,{"derivedFrom":sQuery(id+"F3.wireOp",EDGE,"E28.0.2.8")}),-1.0]])]});
            var Q102;
            Q102=makeQuery(id+"F3.imprint","IMPRINT",FACE,{"disambiguationData":[TD([[makeQuery(id+"F3.imprint","IMPRINT",EDGE,{"derivedFrom":sQuery(id+"F3.wireOp",EDGE,"E28.0.2.4")}),-1.0]])]});
            var Q103;
            Q103=makeQuery(id+"F3.imprint","IMPRINT",FACE,{"disambiguationData":[TD([[makeQuery(id+"F3.imprint","IMPRINT",EDGE,{"derivedFrom":sQuery(id+"F3.wireOp",EDGE,"E28.0.2.32")}),-1.0]])]});
            var Q104;
            Q104=makeQuery(id+"F3.imprint","IMPRINT",FACE,{"disambiguationData":[TD([[makeQuery(id+"F3.imprint","IMPRINT",EDGE,{"derivedFrom":sQuery(id+"F3.wireOp",EDGE,"E28.0.2.17")}),-1.0]])]});
            var Q105;
            Q105=makeQuery(id+"F3.imprint","IMPRINT",FACE,{"disambiguationData":[TD([[makeQuery(id+"F3.imprint","IMPRINT",EDGE,{"derivedFrom":sQuery(id+"F3.wireOp",EDGE,"E28.0.2.21")}),-1.0]])]});
            var Q106;
            Q106=makeQuery(id+"F3.imprint","IMPRINT",FACE,{"disambiguationData":[TD([[makeQuery(id+"F3.imprint","IMPRINT",EDGE,{"derivedFrom":sQuery(id+"F3.wireOp",EDGE,"E28.0.2.38")}),-1.0]])]});
            var Q107;
            Q107=makeQuery(id+"F3.imprint","IMPRINT",FACE,{"disambiguationData":[TD([[makeQuery(id+"F3.imprint","IMPRINT",EDGE,{"derivedFrom":sQuery(id+"F3.wireOp",EDGE,"E28.0.2.7")}),-1.0]])]});
            var Q108;
            Q108=makeQuery(id+"F3.imprint","IMPRINT",FACE,{"disambiguationData":[TD([[makeQuery(id+"F3.imprint","IMPRINT",EDGE,{"derivedFrom":sQuery(id+"F3.wireOp",EDGE,"E28.0.2.15")}),-1.0]])]});
            var Q109;
            Q109=makeQuery(id+"F3.imprint","IMPRINT",FACE,{"disambiguationData":[TD([[makeQuery(id+"F3.imprint","IMPRINT",EDGE,{"derivedFrom":sQuery(id+"F3.wireOp",EDGE,"E28.0.2.23")}),-1.0]])]});
            var Q110;
            Q110=makeQuery(id+"F3.imprint","IMPRINT",FACE,{"disambiguationData":[TD([[makeQuery(id+"F3.imprint","IMPRINT",EDGE,{"derivedFrom":sQuery(id+"F3.wireOp",EDGE,"E28.0.2.28")}),-1.0]])]});
            var Q111;
            Q111=makeQuery(id+"F3.imprint","IMPRINT",FACE,{"disambiguationData":[TD([[makeQuery(id+"F3.imprint","IMPRINT",EDGE,{"derivedFrom":sQuery(id+"F3.wireOp",EDGE,"E28.0.2.60")}),-1.0]])]});
            var Q112;
            Q112=makeQuery(id+"F3.imprint","IMPRINT",FACE,{"disambiguationData":[TD([[makeQuery(id+"F3.imprint","IMPRINT",EDGE,{"derivedFrom":sQuery(id+"F3.wireOp",EDGE,"E28.0.2.3")}),-1.0]])]});
            var Q113;
            Q113=makeQuery(id+"F3.imprint","IMPRINT",FACE,{"disambiguationData":[TD([[makeQuery(id+"F3.imprint","IMPRINT",EDGE,{"derivedFrom":sQuery(id+"F3.wireOp",EDGE,"E28.0.2.34")}),-1.0]])]});
            var Q114;
            Q114=makeQuery(id+"F3.imprint","IMPRINT",FACE,{"disambiguationData":[TD([[makeQuery(id+"F3.imprint","IMPRINT",EDGE,{"derivedFrom":sQuery(id+"F3.wireOp",EDGE,"E28.0.2.22")}),-1.0]])]});
            var Q115;
            Q115=makeQuery(id+"F3.imprint","IMPRINT",FACE,{"disambiguationData":[TD([[makeQuery(id+"F3.imprint","IMPRINT",EDGE,{"derivedFrom":sQuery(id+"F3.wireOp",EDGE,"E28.0.2.52")}),-1.0]])]});
            var Q116;
            Q116=makeQuery(id+"F3.imprint","IMPRINT",FACE,{"disambiguationData":[TD([[makeQuery(id+"F3.imprint","IMPRINT",EDGE,{"derivedFrom":sQuery(id+"F3.wireOp",EDGE,"E28.0.2.12")}),-1.0]])]});
            var Q117;
            Q117=makeQuery(id+"F3.imprint","IMPRINT",FACE,{"disambiguationData":[TD([[makeQuery(id+"F3.imprint","IMPRINT",EDGE,{"derivedFrom":sQuery(id+"F3.wireOp",EDGE,"E28.0.2.0")}),-1.0]])]});
            var Q118;
            Q118=makeQuery(id+"F3.imprint","IMPRINT",FACE,{"disambiguationData":[TD([[makeQuery(id+"F3.imprint","IMPRINT",EDGE,{"derivedFrom":sQuery(id+"F3.wireOp",EDGE,"E28.0.2.37")}),-1.0]])]});
            var Q119;
            Q119=makeQuery(id+"F3.imprint","IMPRINT",FACE,{"disambiguationData":[TD([[makeQuery(id+"F3.imprint","IMPRINT",EDGE,{"derivedFrom":sQuery(id+"F3.wireOp",EDGE,"E28.0.2.78")}),-1.0]])]});
            var Q120;
            Q120=makeQuery(id+"F3.imprint","IMPRINT",FACE,{"disambiguationData":[TD([[makeQuery(id+"F3.imprint","IMPRINT",EDGE,{"derivedFrom":sQuery(id+"F3.wireOp",EDGE,"E28.0.2.24")}),-1.0]])]});
            var Q121;
            Q121=makeQuery(id+"F3.imprint","IMPRINT",FACE,{"disambiguationData":[TD([[makeQuery(id+"F3.imprint","IMPRINT",EDGE,{"derivedFrom":sQuery(id+"F3.wireOp",EDGE,"E28.0.2.20")}),-1.0]])]});
            var Q122;
            Q122=makeQuery(id+"F3.imprint","IMPRINT",FACE,{"disambiguationData":[TD([[makeQuery(id+"F3.imprint","IMPRINT",EDGE,{"derivedFrom":sQuery(id+"F3.wireOp",EDGE,"E28.0.2.47")}),-1.0]])]});
            var Q123;
            Q123=makeQuery(id+"F3.imprint","IMPRINT",FACE,{"disambiguationData":[TD([[makeQuery(id+"F3.imprint","IMPRINT",EDGE,{"derivedFrom":sQuery(id+"F3.wireOp",EDGE,"E28.0.2.57")}),-1.0]])]});
            extrude(context, id + "F4", {"entities" : qUnion([Q0, Q1, Q2, Q3, Q4, Q5, Q6, Q7, Q8, Q9, Q10, Q11, Q12, Q13, Q14, Q15, Q16, Q17, Q18, Q19, Q20, Q21, Q22, Q23, Q24, Q25, Q26, Q27, Q28, Q29, Q30, Q31, Q32, Q33, Q34, Q35, Q36, Q37, Q38, Q39, Q40, Q41, Q42, Q43, Q44, Q45, Q46, Q47, Q48, Q49, Q50, Q51, Q52, Q53, Q54, Q55, Q56, Q57, Q58, Q59, Q60, Q61, Q62, Q63, Q64, Q65, Q66, Q67, Q68, Q69, Q70, Q71, Q72, Q73, Q74, Q75, Q76, Q77, Q78, Q79, Q80, Q81, Q82, Q83, Q84, Q85, Q86, Q87, Q88, Q89, Q90, Q91, Q92, Q93, Q94, Q95, Q96, Q97, Q98, Q99, Q100, Q101, Q102, Q103, Q104, Q105, Q106, Q107, Q108, Q109, Q110, Q111, Q112, Q113, Q114, Q115, Q116, Q117, Q118, Q119, Q120, Q121, Q122, Q123]), "operationType" : NewBodyOperationType.REMOVE, "endBound" : BoundingType.THROUGH_ALL, "oppositeDirection" : true, "depth" : 25 * mm, "offsetDistance" : 25 * mm});
        }
        {
            var Q0;
            Q0 = qSketchRegion(id + "F3", true);
            extrude(context, id + "F5", {"entities" : qUnion([Q0]), "operationType" : NewBodyOperationType.REMOVE, "endBound" : BoundingType.THROUGH_ALL, "depth" : 25 * mm, "offsetDistance" : 25 * mm});
        }
        {
            var Q0;
            Q0=makeQuery(id+"F2.opExtrude","SWEPT_EDGE",EDGE,{"disambiguationData":[OSD([sQuery(id+"F1.wireOp",EDGE,"E4"),sQuery(id+"F1.wireOp",EDGE,"E9")])]});
            chamfer(context, id + "F6", {"entities" : qUnion([Q0]), "chamferType" : ChamferType.TWO_OFFSETS, "width1" : 4 * mm, "oppositeDirection" : false, "width2" : 10 * mm, "tangentPropagation" : true});
        }
        {
            var Q0;
            {var subQ0=sQuery(id+"F1.wireOp",EDGE,"E9");Q0=makeQuery(id+"F6.opChamfer","BLEND_EDGE",EDGE,{"blendedFrom":[makeQuery(id+"F2.opExtrude","SWEPT_EDGE",EDGE,{"disambiguationData":[OSD([sQuery(id+"F1.wireOp",EDGE,"E4"),subQ0])]}),makeQuery(id+"F2.opExtrude","SWEPT_FACE",FACE,{"disambiguationData":[OSD([subQ0])]})],"blendedInto":[makeQuery(id+"F2.opExtrude","SWEPT_FACE",FACE,{"disambiguationData":[OSD([subQ0])]})]});}
            var Q1;
            {var subQ0=sQuery(id+"F1.wireOp",EDGE,"E4");Q1=makeQuery(id+"F6.opChamfer","BLEND_EDGE",EDGE,{"blendedFrom":[makeQuery(id+"F2.opExtrude","SWEPT_EDGE",EDGE,{"disambiguationData":[OSD([subQ0,sQuery(id+"F1.wireOp",EDGE,"E9")])]}),makeQuery(id+"F2.opExtrude","SWEPT_FACE",FACE,{"disambiguationData":[OSD([subQ0])]})],"blendedInto":[makeQuery(id+"F2.opExtrude","SWEPT_FACE",FACE,{"disambiguationData":[OSD([subQ0])]})]});}
            fillet(context, id + "F7", {"entities" : qUnion([Q0, Q1]), "radius" : 5 * mm, "tangentPropagation" : true, "allowEdgeOverflow" : false});
        }
        {
            var Q0;
            Q0=makeQuery(id+"F2.opExtrude","SWEPT_EDGE",EDGE,{"disambiguationData":[OSD([sQuery(id+"F1.wireOp",EDGE,"E11"),sQuery(id+"F1.wireOp",EDGE,"E12")])]});
            var Q1;
            Q1=makeQuery(id+"F2.opExtrude","SWEPT_EDGE",EDGE,{"disambiguationData":[OSD([sQuery(id+"F1.wireOp",EDGE,"E17"),sQuery(id+"F1.wireOp",EDGE,"E18")])]});
            var Q2;
            Q2=makeQuery(id+"F2.opExtrude","SWEPT_EDGE",EDGE,{"disambiguationData":[OSD([sQuery(id+"F1.wireOp",EDGE,"E16"),sQuery(id+"F1.wireOp",EDGE,"E17")])]});
            var Q3;
            Q3=makeQuery(id+"F2.opExtrude","SWEPT_EDGE",EDGE,{"disambiguationData":[OSD([sQuery(id+"F1.wireOp",EDGE,"E19"),sQuery(id+"F1.wireOp",EDGE,"E20")])]});
            var Q4;
            Q4=makeQuery(id+"F2.opExtrude","SWEPT_EDGE",EDGE,{"disambiguationData":[OSD([sQuery(id+"F1.wireOp",EDGE,"E13"),sQuery(id+"F1.wireOp",EDGE,"E19")])]});
            var Q5;
            Q5=makeQuery(id+"F2.opExtrude","SWEPT_EDGE",EDGE,{"disambiguationData":[OSD([sQuery(id+"F1.wireOp",EDGE,"E10"),sQuery(id+"F1.wireOp",EDGE,"E12")])]});
            var Q6;
            Q6=makeQuery(id+"F2.opExtrude","SWEPT_EDGE",EDGE,{"disambiguationData":[OSD([sQuery(id+"F1.wireOp",EDGE,"E15"),sQuery(id+"F1.wireOp",EDGE,"E18")])]});
            var Q7;
            Q7=makeQuery(id+"F2.opExtrude","SWEPT_EDGE",EDGE,{"disambiguationData":[OSD([sQuery(id+"F1.wireOp",EDGE,"E13"),sQuery(id+"F1.wireOp",EDGE,"E14")])]});
            var Q8;
            Q8=makeQuery(id+"F2.opExtrude","SWEPT_EDGE",EDGE,{"disambiguationData":[OSD([sQuery(id+"F1.wireOp",EDGE,"E10"),sQuery(id+"F1.wireOp",EDGE,"E11")])]});
            var Q9;
            Q9=makeQuery(id+"F2.opExtrude","SWEPT_EDGE",EDGE,{"disambiguationData":[OSD([sQuery(id+"F1.wireOp",EDGE,"E15"),sQuery(id+"F1.wireOp",EDGE,"E16")])]});
            var Q10;
            Q10=makeQuery(id+"F2.opExtrude","SWEPT_EDGE",EDGE,{"disambiguationData":[OSD([sQuery(id+"F1.wireOp",EDGE,"E14"),sQuery(id+"F1.wireOp",EDGE,"E20")])]});
            var Q11;
            Q11=makeQuery(id+"F2.opExtrude","SWEPT_EDGE",EDGE,{"disambiguationData":[OSD([sQuery(id+"F1.wireOp",EDGE,"E5"),sQuery(id+"F1.wireOp",EDGE,"E6")])]});
            var Q12;
            Q12=makeQuery(id+"F2.opExtrude","SWEPT_EDGE",EDGE,{"disambiguationData":[OSD([sQuery(id+"F1.wireOp",EDGE,"E4"),sQuery(id+"F1.wireOp",EDGE,"E5")])]});
            var Q13;
            Q13=makeQuery(id+"F2.opExtrude","SWEPT_EDGE",EDGE,{"disambiguationData":[OSD([sQuery(id+"F1.wireOp",EDGE,"E4"),sQuery(id+"F1.wireOp",EDGE,"E6"),sQuery(id+"F1.wireOp",EDGE,"E7")])]});
            fillet(context, id + "F8", {"entities" : qUnion([Q0, Q1, Q2, Q3, Q4, Q5, Q6, Q7, Q8, Q9, Q10, Q11, Q12, Q13]), "radius" : 3 * mm, "tangentPropagation" : true, "allowEdgeOverflow" : false});
        }
        {
            var Q0;
            Q0=makeQuery(id+"F2.opExtrude","SWEPT_EDGE",EDGE,{"disambiguationData":[OSD([sQuery(id+"F1.wireOp",EDGE,"E8"),sQuery(id+"F1.wireOp",EDGE,"E9")])]});
            var Q1;
            Q1=makeQuery(id+"F2.opExtrude","SWEPT_EDGE",EDGE,{"disambiguationData":[OSD([sQuery(id+"F1.wireOp",EDGE,"E7"),sQuery(id+"F1.wireOp",EDGE,"E8")])]});
            var Q2;
            Q2=makeQuery(id+"F2.opExtrude","CAP_EDGE",EDGE,{"disambiguationData":[OSD([sQuery(id+"F1.wireOp",EDGE,"E4")])],"isStart":false});
            var Q3;
            Q3=makeQuery(id+"F2.opExtrude","CAP_EDGE",EDGE,{"disambiguationData":[OSD([sQuery(id+"F1.wireOp",EDGE,"E11")])],"isStart":false});
            var Q4;
            Q4=makeQuery(id+"F2.opExtrude","CAP_EDGE",EDGE,{"disambiguationData":[OSD([sQuery(id+"F1.wireOp",EDGE,"E16")])],"isStart":false});
            var Q5;
            Q5=makeQuery(id+"F2.opExtrude","CAP_EDGE",EDGE,{"disambiguationData":[OSD([sQuery(id+"F1.wireOp",EDGE,"E20")])],"isStart":false});
            var Q6;
            Q6=makeQuery(id+"F2.opExtrude","CAP_EDGE",EDGE,{"disambiguationData":[OSD([sQuery(id+"F1.wireOp",EDGE,"E20")])],"isStart":true});
            var Q7;
            Q7=makeQuery(id+"F2.opExtrude","CAP_EDGE",EDGE,{"disambiguationData":[OSD([sQuery(id+"F1.wireOp",EDGE,"E16")])],"isStart":true});
            var Q8;
            Q8=makeQuery(id+"F2.opExtrude","CAP_EDGE",EDGE,{"disambiguationData":[OSD([sQuery(id+"F1.wireOp",EDGE,"E11")])],"isStart":true});
            var Q9;
            Q9=makeQuery(id+"F2.opExtrude","CAP_EDGE",EDGE,{"disambiguationData":[OSD([sQuery(id+"F1.wireOp",EDGE,"E6")])],"isStart":true});
            fillet(context, id + "F9", {"entities" : qUnion([Q0, Q1, Q2, Q3, Q4, Q5, Q6, Q7, Q8, Q9]), "radius" : 1 * mm, "tangentPropagation" : true, "allowEdgeOverflow" : false});
        }
        {
            var Q0;
            Q0=makeQuery(id+"F5.boolean.opBoolean","INTERSECT",EDGE,{"derivedFrom":[makeQuery(id+"F2.opExtrude","SWEPT_FACE",FACE,{"disambiguationData":[OSD([sQuery(id+"F1.wireOp",EDGE,"E4")])]}),makeQuery(id+"F5.opExtrude","SWEPT_FACE",FACE,{"disambiguationData":[OSD([sQuery(id+"F3.wireOp",EDGE,"E27.0.2.3")])]})]});
            var Q1;
            Q1=makeQuery(id+"F5.boolean.opBoolean","INTERSECT",EDGE,{"derivedFrom":[makeQuery(id+"F2.opExtrude","SWEPT_FACE",FACE,{"disambiguationData":[OSD([sQuery(id+"F1.wireOp",EDGE,"E4")])]}),makeQuery(id+"F5.opExtrude","SWEPT_FACE",FACE,{"disambiguationData":[OSD([sQuery(id+"F3.wireOp",EDGE,"E27.0.2.2")])]})]});
            var Q2;
            Q2=makeQuery(id+"F5.boolean.opBoolean","INTERSECT",EDGE,{"derivedFrom":[makeQuery(id+"F2.opExtrude","SWEPT_FACE",FACE,{"disambiguationData":[OSD([sQuery(id+"F1.wireOp",EDGE,"E4")])]}),makeQuery(id+"F5.opExtrude","SWEPT_FACE",FACE,{"disambiguationData":[OSD([sQuery(id+"F3.wireOp",EDGE,"E27.0.2.5")])]})]});
            var Q3;
            Q3=makeQuery(id+"F5.boolean.opBoolean","INTERSECT",EDGE,{"derivedFrom":[makeQuery(id+"F2.opExtrude","SWEPT_FACE",FACE,{"disambiguationData":[OSD([sQuery(id+"F1.wireOp",EDGE,"E4")])]}),makeQuery(id+"F5.opExtrude","SWEPT_FACE",FACE,{"disambiguationData":[OSD([sQuery(id+"F3.wireOp",EDGE,"E22")])]})]});
            var Q4;
            Q4=makeQuery(id+"F5.boolean.opBoolean","INTERSECT",EDGE,{"derivedFrom":[makeQuery(id+"F2.opExtrude","SWEPT_FACE",FACE,{"disambiguationData":[OSD([sQuery(id+"F1.wireOp",EDGE,"E4")])]}),makeQuery(id+"F5.opExtrude","SWEPT_FACE",FACE,{"disambiguationData":[OSD([sQuery(id+"F3.wireOp",EDGE,"E21")])]})]});
            var Q5;
            Q5=makeQuery(id+"F5.boolean.opBoolean","INTERSECT",EDGE,{"derivedFrom":[makeQuery(id+"F2.opExtrude","SWEPT_FACE",FACE,{"disambiguationData":[OSD([sQuery(id+"F1.wireOp",EDGE,"E4")])]}),makeQuery(id+"F5.opExtrude","SWEPT_FACE",FACE,{"disambiguationData":[OSD([sQuery(id+"F3.wireOp",EDGE,"E23")])]})]});
            var Q6;
            Q6=makeQuery(id+"F5.boolean.opBoolean","INTERSECT",EDGE,{"derivedFrom":[makeQuery(id+"F2.opExtrude","SWEPT_FACE",FACE,{"disambiguationData":[OSD([sQuery(id+"F1.wireOp",EDGE,"E4")])]}),makeQuery(id+"F5.opExtrude","SWEPT_FACE",FACE,{"disambiguationData":[OSD([sQuery(id+"F3.wireOp",EDGE,"E27.0.1.2")])]})]});
            var Q7;
            Q7=makeQuery(id+"F5.boolean.opBoolean","INTERSECT",EDGE,{"derivedFrom":[makeQuery(id+"F2.opExtrude","SWEPT_FACE",FACE,{"disambiguationData":[OSD([sQuery(id+"F1.wireOp",EDGE,"E4")])]}),makeQuery(id+"F5.opExtrude","SWEPT_FACE",FACE,{"disambiguationData":[OSD([sQuery(id+"F3.wireOp",EDGE,"E27.0.1.5")])]})]});
            var Q8;
            Q8=makeQuery(id+"F5.boolean.opBoolean","INTERSECT",EDGE,{"derivedFrom":[makeQuery(id+"F2.opExtrude","SWEPT_FACE",FACE,{"disambiguationData":[OSD([sQuery(id+"F1.wireOp",EDGE,"E4")])]}),makeQuery(id+"F5.opExtrude","SWEPT_FACE",FACE,{"disambiguationData":[OSD([sQuery(id+"F3.wireOp",EDGE,"E27.0.1.3")])]})]});
            var Q9;
            Q9=makeQuery(id+"F5.boolean.opBoolean","INTERSECT",EDGE,{"derivedFrom":[makeQuery(id+"F2.opExtrude","SWEPT_FACE",FACE,{"disambiguationData":[OSD([sQuery(id+"F1.wireOp",EDGE,"E4")])]}),makeQuery(id+"F5.opExtrude","SWEPT_FACE",FACE,{"disambiguationData":[OSD([sQuery(id+"F3.wireOp",EDGE,"E26")])]})]});
            var Q10;
            Q10=makeQuery(id+"F5.boolean.opBoolean","INTERSECT",EDGE,{"derivedFrom":[makeQuery(id+"F2.opExtrude","SWEPT_FACE",FACE,{"disambiguationData":[OSD([sQuery(id+"F1.wireOp",EDGE,"E4")])]}),makeQuery(id+"F5.opExtrude","SWEPT_FACE",FACE,{"disambiguationData":[OSD([sQuery(id+"F3.wireOp",EDGE,"E24")])]})]});
            var Q11;
            Q11=makeQuery(id+"F5.boolean.opBoolean","INTERSECT",EDGE,{"derivedFrom":[makeQuery(id+"F2.opExtrude","SWEPT_FACE",FACE,{"disambiguationData":[OSD([sQuery(id+"F1.wireOp",EDGE,"E4")])]}),makeQuery(id+"F5.opExtrude","SWEPT_FACE",FACE,{"disambiguationData":[OSD([sQuery(id+"F3.wireOp",EDGE,"E25")])]})]});
            var Q12;
            Q12=makeQuery(id+"F5.boolean.opBoolean","INTERSECT",EDGE,{"derivedFrom":[makeQuery(id+"F2.opExtrude","SWEPT_FACE",FACE,{"disambiguationData":[OSD([sQuery(id+"F1.wireOp",EDGE,"E4")])]}),makeQuery(id+"F5.opExtrude","SWEPT_FACE",FACE,{"disambiguationData":[OSD([sQuery(id+"F3.wireOp",EDGE,"E27.0.1.4")])]})]});
            var Q13;
            Q13=makeQuery(id+"F5.boolean.opBoolean","INTERSECT",EDGE,{"derivedFrom":[makeQuery(id+"F2.opExtrude","SWEPT_FACE",FACE,{"disambiguationData":[OSD([sQuery(id+"F1.wireOp",EDGE,"E4")])]}),makeQuery(id+"F5.opExtrude","SWEPT_FACE",FACE,{"disambiguationData":[OSD([sQuery(id+"F3.wireOp",EDGE,"E27.0.1.1")])]})]});
            var Q14;
            Q14=makeQuery(id+"F5.boolean.opBoolean","INTERSECT",EDGE,{"derivedFrom":[makeQuery(id+"F2.opExtrude","SWEPT_FACE",FACE,{"disambiguationData":[OSD([sQuery(id+"F1.wireOp",EDGE,"E4")])]}),makeQuery(id+"F5.opExtrude","SWEPT_FACE",FACE,{"disambiguationData":[OSD([sQuery(id+"F3.wireOp",EDGE,"E27.0.1.0")])]})]});
            var Q15;
            Q15=makeQuery(id+"F5.boolean.opBoolean","INTERSECT",EDGE,{"derivedFrom":[makeQuery(id+"F2.opExtrude","SWEPT_FACE",FACE,{"disambiguationData":[OSD([sQuery(id+"F1.wireOp",EDGE,"E4")])]}),makeQuery(id+"F5.opExtrude","SWEPT_FACE",FACE,{"disambiguationData":[OSD([sQuery(id+"F3.wireOp",EDGE,"E27.0.2.1")])]})]});
            var Q16;
            Q16=makeQuery(id+"F5.boolean.opBoolean","INTERSECT",EDGE,{"derivedFrom":[makeQuery(id+"F2.opExtrude","SWEPT_FACE",FACE,{"disambiguationData":[OSD([sQuery(id+"F1.wireOp",EDGE,"E4")])]}),makeQuery(id+"F5.opExtrude","SWEPT_FACE",FACE,{"disambiguationData":[OSD([sQuery(id+"F3.wireOp",EDGE,"E27.0.2.4")])]})]});
            var Q17;
            Q17=makeQuery(id+"F5.boolean.opBoolean","INTERSECT",EDGE,{"derivedFrom":[makeQuery(id+"F2.opExtrude","SWEPT_FACE",FACE,{"disambiguationData":[OSD([sQuery(id+"F1.wireOp",EDGE,"E4")])]}),makeQuery(id+"F5.opExtrude","SWEPT_FACE",FACE,{"disambiguationData":[OSD([sQuery(id+"F3.wireOp",EDGE,"E27.0.2.0")])]})]});
            var Q18;
            Q18=makeQuery(id+"F5.boolean.opBoolean","INTERSECT",EDGE,{"derivedFrom":[makeQuery(id+"F2.opExtrude","SWEPT_FACE",FACE,{"disambiguationData":[OSD([sQuery(id+"F1.wireOp",EDGE,"E4")])]}),makeQuery(id+"F5.opExtrude","SWEPT_FACE",FACE,{"disambiguationData":[OSD([sQuery(id+"F3.wireOp",EDGE,"E27.1.2.5")])]})]});
            var Q19;
            Q19=makeQuery(id+"F5.boolean.opBoolean","INTERSECT",EDGE,{"derivedFrom":[makeQuery(id+"F2.opExtrude","SWEPT_FACE",FACE,{"disambiguationData":[OSD([sQuery(id+"F1.wireOp",EDGE,"E4")])]}),makeQuery(id+"F5.opExtrude","SWEPT_FACE",FACE,{"disambiguationData":[OSD([sQuery(id+"F3.wireOp",EDGE,"E27.1.2.2")])]})]});
            var Q20;
            Q20=makeQuery(id+"F5.boolean.opBoolean","INTERSECT",EDGE,{"derivedFrom":[makeQuery(id+"F2.opExtrude","SWEPT_FACE",FACE,{"disambiguationData":[OSD([sQuery(id+"F1.wireOp",EDGE,"E4")])]}),makeQuery(id+"F5.opExtrude","SWEPT_FACE",FACE,{"disambiguationData":[OSD([sQuery(id+"F3.wireOp",EDGE,"E27.1.2.3")])]})]});
            var Q21;
            Q21=makeQuery(id+"F5.boolean.opBoolean","INTERSECT",EDGE,{"derivedFrom":[makeQuery(id+"F2.opExtrude","SWEPT_FACE",FACE,{"disambiguationData":[OSD([sQuery(id+"F1.wireOp",EDGE,"E4")])]}),makeQuery(id+"F5.opExtrude","SWEPT_FACE",FACE,{"disambiguationData":[OSD([sQuery(id+"F3.wireOp",EDGE,"E27.1.2.1")])]})]});
            var Q22;
            Q22=makeQuery(id+"F5.boolean.opBoolean","INTERSECT",EDGE,{"derivedFrom":[makeQuery(id+"F2.opExtrude","SWEPT_FACE",FACE,{"disambiguationData":[OSD([sQuery(id+"F1.wireOp",EDGE,"E4")])]}),makeQuery(id+"F5.opExtrude","SWEPT_FACE",FACE,{"disambiguationData":[OSD([sQuery(id+"F3.wireOp",EDGE,"E27.1.2.4")])]})]});
            var Q23;
            Q23=makeQuery(id+"F5.boolean.opBoolean","INTERSECT",EDGE,{"derivedFrom":[makeQuery(id+"F2.opExtrude","SWEPT_FACE",FACE,{"disambiguationData":[OSD([sQuery(id+"F1.wireOp",EDGE,"E4")])]}),makeQuery(id+"F5.opExtrude","SWEPT_FACE",FACE,{"disambiguationData":[OSD([sQuery(id+"F3.wireOp",EDGE,"E27.1.2.0")])]})]});
            var Q24;
            Q24=makeQuery(id+"F5.boolean.opBoolean","INTERSECT",EDGE,{"derivedFrom":[makeQuery(id+"F2.opExtrude","SWEPT_FACE",FACE,{"disambiguationData":[OSD([sQuery(id+"F1.wireOp",EDGE,"E4")])]}),makeQuery(id+"F5.opExtrude","SWEPT_FACE",FACE,{"disambiguationData":[OSD([sQuery(id+"F3.wireOp",EDGE,"E27.2.2.5")])]})]});
            var Q25;
            Q25=makeQuery(id+"F5.boolean.opBoolean","INTERSECT",EDGE,{"derivedFrom":[makeQuery(id+"F2.opExtrude","SWEPT_FACE",FACE,{"disambiguationData":[OSD([sQuery(id+"F1.wireOp",EDGE,"E4")])]}),makeQuery(id+"F5.opExtrude","SWEPT_FACE",FACE,{"disambiguationData":[OSD([sQuery(id+"F3.wireOp",EDGE,"E27.2.2.2")])]})]});
            var Q26;
            Q26=makeQuery(id+"F5.boolean.opBoolean","INTERSECT",EDGE,{"derivedFrom":[makeQuery(id+"F2.opExtrude","SWEPT_FACE",FACE,{"disambiguationData":[OSD([sQuery(id+"F1.wireOp",EDGE,"E4")])]}),makeQuery(id+"F5.opExtrude","SWEPT_FACE",FACE,{"disambiguationData":[OSD([sQuery(id+"F3.wireOp",EDGE,"E27.2.2.3")])]})]});
            var Q27;
            Q27=makeQuery(id+"F2.opExtrude","SWEPT_FACE",FACE,{"disambiguationData":[OSD([sQuery(id+"F1.wireOp",EDGE,"E4")])]});
            var Q28;
            Q28=makeQuery(id+"F5.boolean.opBoolean","INTERSECT",EDGE,{"derivedFrom":[makeQuery(id+"F2.opExtrude","SWEPT_FACE",FACE,{"disambiguationData":[OSD([sQuery(id+"F1.wireOp",EDGE,"E4")])]}),makeQuery(id+"F5.opExtrude","SWEPT_FACE",FACE,{"disambiguationData":[OSD([sQuery(id+"F3.wireOp",EDGE,"E27.1.1.2")])]})]});
            var Q29;
            Q29=makeQuery(id+"F5.boolean.opBoolean","INTERSECT",EDGE,{"derivedFrom":[makeQuery(id+"F2.opExtrude","SWEPT_FACE",FACE,{"disambiguationData":[OSD([sQuery(id+"F1.wireOp",EDGE,"E4")])]}),makeQuery(id+"F5.opExtrude","SWEPT_FACE",FACE,{"disambiguationData":[OSD([sQuery(id+"F3.wireOp",EDGE,"E27.1.1.3")])]})]});
            fillet(context, id + "F10", {"entities" : qUnion([Q0, Q1, Q2, Q3, Q4, Q5, Q6, Q7, Q8, Q9, Q10, Q11, Q12, Q13, Q14, Q15, Q16, Q17, Q18, Q19, Q20, Q21, Q22, Q23, Q24, Q25, Q26, Q27, Q28, Q29]), "radius" : 1 * mm, "tangentPropagation" : true, "allowEdgeOverflow" : false});
        }
    });
